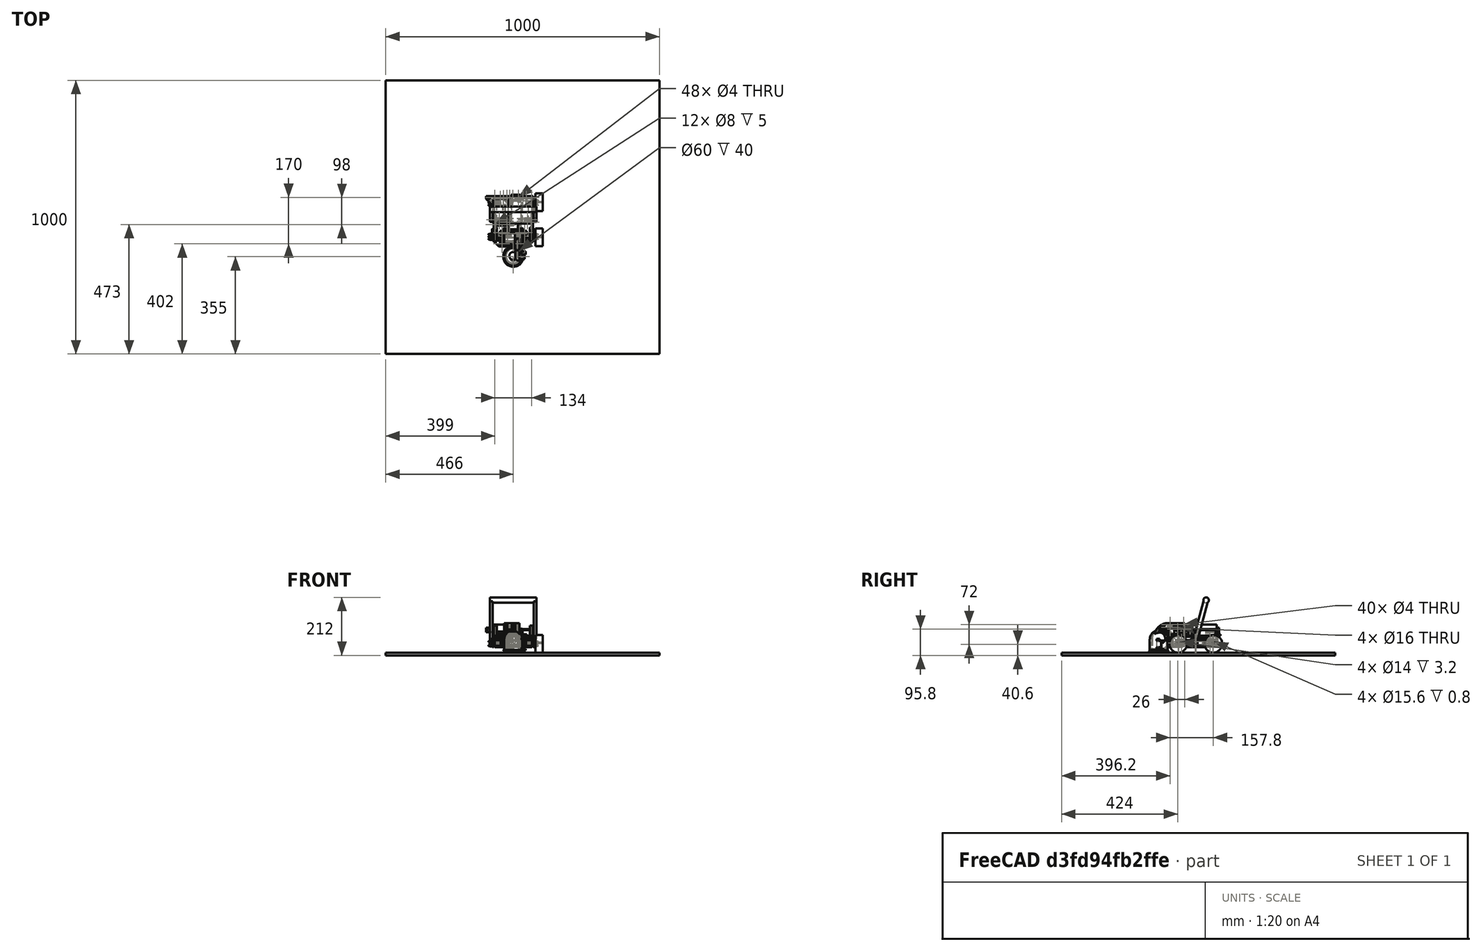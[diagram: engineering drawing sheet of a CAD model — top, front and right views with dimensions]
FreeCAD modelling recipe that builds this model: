
FCSTD DOCUMENT  (FreeCAD 1.0R39109 (Git))
Label: robot - robcup-ber3.2
License: All rights reserved
LicenseURL: https://en.wikipedia.org/wiki/All_rights_reserved
objects: Part::Cylinder×204, Part::Box×156, Part::Cut×138, Part::MultiFuse×132, Part::FeaturePython×20, Part::Chamfer×15, Part::Sphere×10, Part::Fillet×10, Part::Cone×6, Part::Extrusion×4, Part::Part2DObjectPython×2, Part::Fuse×2, Part::RuledSurface×2
note: 701 computed .brp shape members not serialized (recipe doc carries the construction recipe); baked Part::Feature solids carry a one-line shape summary decoded from their .brp

FEATURE [Part::Box] Box001  label="rasbperry pi"
  AttacherType = Attacher::AttachEngine3D
  Height = 25
  Length = 56
  Placement = pos=(-108,-22,52) rot=(0,0,1;0rad)
  Width = 88
FEATURE [Part::Box] Box024  label="立方体004"
  AttacherType = Attacher::AttachEngine3D
  Height = 25
  Length = 51
  Placement = pos=(-51,-93,16) rot=(0,0,1;0rad)
  Width = 5
FEATURE [Part::Box] Box025  label="立方体005"
  AttacherType = Attacher::AttachEngine3D
  Height = 25
  Length = 23
  Placement = pos=(-37,-93,16) rot=(0,0,1;0rad)
  Width = 5
FEATURE [Part::Box] Box026  label="立方体006"
  AttacherType = Attacher::AttachEngine3D
  Height = 10
  Length = 51
  Placement = pos=(-51,-90,31) rot=(0,0,1;0rad)
  Width = 5
FEATURE [Part::Box] Box027  label="立方体007"
  AttacherType = Attacher::AttachEngine3D
  Height = 20.4
  Length = 45.2
  Placement = pos=(-48.6,-98,10) rot=(0,0,1;0rad)
  Width = 5
FEATURE [Part::Cylinder] Cylinder004  label="円柱004"
  Angle = 360
  AttacherType = Attacher::AttachEngine3D
  FirstAngle = 0
  Height = 15
  Placement = pos=(-13,-93,20.2) rot=(1,0,0;1.5708rad)
  Radius = 8
  SecondAngle = 0
FEATURE [Part::Cylinder] Cylinder005  label="円柱005"
  Angle = 360
  AttacherType = Attacher::AttachEngine3D
  FirstAngle = 0
  Height = 15
  Placement = pos=(-39,-93,20.2) rot=(1,0,0;1.5708rad)
  Radius = 8
  SecondAngle = 0
FEATURE [Part::Cylinder] Cylinder007  label="円柱007"
  Angle = 360
  AttacherType = Attacher::AttachEngine3D
  FirstAngle = 0
  Height = 32
  Placement = pos=(0,82,0) rot=(0,0,1;0rad)
  Radius = 4
  SecondAngle = 0
FEATURE [Part::Cylinder] Cylinder011  label="円柱011"
  Angle = 360
  AttacherType = Attacher::AttachEngine3D
  FirstAngle = 0
  Height = 32
  Placement = pos=(15.2,-98,0) rot=(0,0,1;0rad)
  Radius = 4
  SecondAngle = 0
FEATURE [Part::Cylinder] Cylinder012  label="円柱012"
  Angle = 360
  AttacherType = Attacher::AttachEngine3D
  FirstAngle = 0
  Height = 42
  Placement = pos=(-68,82,-5) rot=(0,0,1;0rad)
  Radius = 2
  SecondAngle = 0
FEATURE [Part::Cylinder] Cylinder016  label="円柱016"
  Angle = 360
  AttacherType = Attacher::AttachEngine3D
  FirstAngle = 0
  Height = 32
  Placement = pos=(-83,-98,0) rot=(0,0,1;0rad)
  Radius = 4
  SecondAngle = 0
FEATURE [Part::Box] Box060  label="（バッテリー）"
  AttacherType = Attacher::AttachEngine3D
  Height = 26.5
  Length = 58
  Placement = pos=(-62.9,-27,0) rot=(0,0,1;0rad)
  Width = 81.5
FEATURE [Part::Box] Box069  label="立方体048"
  AttacherType = Attacher::AttachEngine3D
  Height = 20.1
  Length = 38.8
  Placement = pos=(82,-93,0) rot=(0,0,1;0rad)
  Width = 40.1
FEATURE [Part::Box] Box075  label="立方体054"
  AttacherType = Attacher::AttachEngine3D
  Height = 20.1
  Length = 38.8
  Placement = pos=(82,-93,0) rot=(0,0,1;0rad)
  Width = 40.1
FEATURE [Part::Box] Box084  label="立方体063"
  AttacherType = Attacher::AttachEngine3D
  Height = 20.1
  Length = 2.7
  Placement = pos=(90.8,-99.95,0) rot=(0,0,1;0rad)
  Width = 54
FEATURE [Part::MultiFuse] Fusion040
  Placement = pos=(-7.9,-3,-13) rot=(0,0,1;0rad)
  Refine = true
  Shapes = -> [Box027,Cylinder004,Cylinder005]
FEATURE [Part::Box] Box097  label="立方体076"
  AttacherType = Attacher::AttachEngine3D
  Height = 25
  Length = 52
  Placement = pos=(-60,-93,16) rot=(0,0,1;0rad)
  Width = 5
FEATURE [Part::Box] Box098  label="立方体077"
  AttacherType = Attacher::AttachEngine3D
  Height = 25
  Length = 35
  Placement = pos=(-52,-88,16) rot=(0,0,1;0rad)
  Width = 5
FEATURE [Part::Box] Box100  label="立方体079"
  AttacherType = Attacher::AttachEngine3D
  Height = 25
  Length = 25
  Placement = pos=(-38.5,-94,16) rot=(0,0,1;0rad)
  Width = 1
FEATURE [Part::Box] Box101  label="立方体080"
  AttacherType = Attacher::AttachEngine3D
  Height = 25
  Length = 15
  Placement = pos=(-33.5,-101,16) rot=(0,0,1;0rad)
  Width = 7
FEATURE [Part::Box] Box102  label="立方体081"
  AttacherType = Attacher::AttachEngine3D
  Height = 5
  Length = 60
  Placement = pos=(-63.9,-96,-5) rot=(0,0,1;0rad)
  Width = 64
FEATURE [Part::Cylinder] Cylinder033  label="円柱033"
  Angle = 360
  AttacherType = Attacher::AttachEngine3D
  FirstAngle = 0
  Height = 32
  Placement = pos=(30.2,-10,0) rot=(0,0,1;0rad)
  Radius = 4
  SecondAngle = 0
FEATURE [Part::Cylinder] Cylinder034  label="円柱034"
  Angle = 360
  AttacherType = Attacher::AttachEngine3D
  FirstAngle = 0
  Height = 32
  Placement = pos=(-98,-10,0) rot=(0,0,1;0rad)
  Radius = 4
  SecondAngle = 0
FEATURE [Part::Box] Box213  label="立方体191"
  AttacherType = Attacher::AttachEngine3D
  Height = 12
  Length = 3
  Placement = pos=(-65.9,-16.9,0) rot=(0,0,1;0rad)
  Width = 13.9
FEATURE [Part::Box] Box214  label="立方体192"
  AttacherType = Attacher::AttachEngine3D
  Height = 12
  Length = 3
  Placement = pos=(-4.9,-16.9,0) rot=(0,0,1;0rad)
  Width = 13.9
FEATURE [Part::Box] Box215  label="立方体193"
  AttacherType = Attacher::AttachEngine3D
  Height = 5
  Length = 54
  Placement = pos=(-60.9,-108,32) rot=(0,0,1;0rad)
  Width = 71
FEATURE [Part::Box] Box223  label="立方体201"
  AttacherType = Attacher::AttachEngine3D
  Height = 20.1
  Length = 2.7
  Placement = pos=(90.8,-99.95,0) rot=(0,0,1;0rad)
  Width = 54
FEATURE [Part::Box] Box225  label="立方体203"
  AttacherType = Attacher::AttachEngine3D
  Height = 20.1
  Length = 2.7
  Placement = pos=(109.3,-99.95,0) rot=(0,0,1;0rad)
  Width = 54
FEATURE [Part::MultiFuse] Fusion084
  Placement = pos=(-188,26,0) rot=(0,0,1;0rad)
  Shapes = -> [Box084,Box069]
FEATURE [Part::MultiFuse] Fusion085
  Placement = pos=(-188,100,0) rot=(0,0,1;0rad)
  Shapes = -> [Box223,Box075]
FEATURE [Part::Box] Box226  label="立方体204"
  AttacherType = Attacher::AttachEngine3D
  Height = 20.1
  Length = 38.8
  Placement = pos=(82,-93,0) rot=(0,0,1;0rad)
  Width = 40.1
FEATURE [Part::Box] Box227  label="立方体205"
  AttacherType = Attacher::AttachEngine3D
  Height = 20.1
  Length = 38.8
  Placement = pos=(82,-93,0) rot=(0,0,1;0rad)
  Width = 40.1
FEATURE [Part::MultiFuse] Fusion086
  Placement = pos=(-82.6,26,0) rot=(0,0,1;0rad)
  Shapes = -> [Box226,Box225]
FEATURE [Part::Box] Box076  label="立方体055"
  AttacherType = Attacher::AttachEngine3D
  Height = 20.1
  Length = 2.7
  Placement = pos=(109.3,-99.95,0) rot=(0,0,1;0rad)
  Width = 54
FEATURE [Part::MultiFuse] Fusion087
  Placement = pos=(-82.6,100,0) rot=(0,0,1;0rad)
  Shapes = -> [Box076,Box227]
FEATURE [Part::Box] Box229  label="立方体208"
  AttacherType = Attacher::AttachEngine3D
  Height = 20
  Length = 10
  Placement = pos=(16.7,47.1,0) rot=(0,0,1;0rad)
  Width = 7
FEATURE [Part::Box] Box235  label="立方体214"
  AttacherType = Attacher::AttachEngine3D
  Height = 12
  Length = 58.6
  Placement = pos=(-63.2,-30,0) rot=(0,0,1;0rad)
  Width = 3
FEATURE [Part::Box] Box242  label="立方体220"
  AttacherType = Attacher::AttachEngine3D
  Height = 20
  Length = 21.5
  Placement = pos=(16,57.1,0) rot=(0,0,1;0rad)
  Width = 13
FEATURE [Part::Box] Box254  label="立方体229"
  AttacherType = Attacher::AttachEngine3D
  Height = 22
  Length = 54
  Placement = pos=(-60.9,-108,-3) rot=(0,0,1;0rad)
  Width = 12
FEATURE [Part::FeaturePython] CycloidGear  # WARN: FeaturePython — macro-defined, semantics opaque (R4)
  AttacherType = Attacher::AttachEngine3D
  Placement = pos=(-32.8,-91,71) rot=(0,1,0;1.5708rad)
  angular_backlash = 0
  backlash = 0
  clearance = 0.25
  double_helix = false
  head = 0
  head_fillet = 0
  height = 5.5
  helix_angle = 0
  inner_diameter = 12.5
  module = 0.24
  num_teeth = 25
  numpoints = 20
  outer_diameter = 7.5
  pitch_diameter = 6
  root_fillet = 0
  version = 1.3.0
  expr: angular_backlash = backlash / pitch_diameter * 360 ° / pi
  expr: inner_diameter = num_teeth / 2
  expr: pitch_diameter = num_teeth * module
FEATURE [Part::Box] Box259  label="立方体234"
  AttacherType = Attacher::AttachEngine3D
  Height = 3
  Length = 90
  Placement = pos=(-52,-40,42) rot=(0,0,1;0rad)
  Width = 100
FEATURE [Part::Box] Box260  label="立方体235"
  AttacherType = Attacher::AttachEngine3D
  Height = 3
  Length = 56
  Placement = pos=(-104,-22,37) rot=(0,0,1;0rad)
  Width = 88
FEATURE [Part::Cylinder] Cylinder064  label="円柱064"
  Angle = 360
  AttacherType = Attacher::AttachEngine3D
  FirstAngle = 0
  Height = 3
  Placement = pos=(-100.5,62.5,37) rot=(0,0,1;0rad)
  Radius = 1.25
  SecondAngle = 0
FEATURE [Part::Cylinder] Cylinder065  label="円柱065"
  Angle = 360
  AttacherType = Attacher::AttachEngine3D
  FirstAngle = 0
  Height = 3
  Placement = pos=(-51.5,62.5,37) rot=(0,0,1;0rad)
  Radius = 1.25
  SecondAngle = 0
FEATURE [Part::Cylinder] Cylinder066  label="円柱066"
  Angle = 360
  AttacherType = Attacher::AttachEngine3D
  FirstAngle = 0
  Height = 3
  Placement = pos=(-51.5,4.5,37) rot=(0,0,1;0rad)
  Radius = 1.25
  SecondAngle = 0
FEATURE [Part::Cylinder] Cylinder067  label="円柱067"
  Angle = 360
  AttacherType = Attacher::AttachEngine3D
  FirstAngle = 0
  Height = 3
  Placement = pos=(-100.5,4.5,37) rot=(0,0,1;0rad)
  Radius = 1.25
  SecondAngle = 0
FEATURE [Part::Box] Box263  label="立方体237"
  AttacherType = Attacher::AttachEngine3D
  Height = 20.4
  Length = 45.2
  Placement = pos=(-48.6,-98,10) rot=(0,0,1;0rad)
  Width = 5
FEATURE [Part::Cylinder] Cylinder068  label="円柱068"
  Angle = 360
  AttacherType = Attacher::AttachEngine3D
  FirstAngle = 0
  Height = 15
  Placement = pos=(-13,-93,20.2) rot=(1,0,0;1.5708rad)
  Radius = 8
  SecondAngle = 0
FEATURE [Part::Cylinder] Cylinder069  label="円柱069"
  Angle = 360
  AttacherType = Attacher::AttachEngine3D
  FirstAngle = 0
  Height = 15
  Placement = pos=(-39,-93,20.2) rot=(1,0,0;1.5708rad)
  Radius = 8
  SecondAngle = 0
FEATURE [Part::MultiFuse] Fusion112
  Placement = pos=(-1,-109,40) rot=(0,0,-1;1.5708rad)
  Refine = true
  Shapes = -> [Box263,Cylinder069,Cylinder068]
FEATURE [Part::Box] Box264  label="立方体238"
  AttacherType = Attacher::AttachEngine3D
  Height = 20.4
  Length = 45.2
  Placement = pos=(-48.6,-98,10) rot=(0,0,1;0rad)
  Width = 5
FEATURE [Part::Cylinder] Cylinder070  label="円柱070"
  Angle = 360
  AttacherType = Attacher::AttachEngine3D
  FirstAngle = 0
  Height = 15
  Placement = pos=(-13,-93,20.2) rot=(1,0,0;1.5708rad)
  Radius = 8
  SecondAngle = 0
FEATURE [Part::Cylinder] Cylinder071  label="円柱071"
  Angle = 360
  AttacherType = Attacher::AttachEngine3D
  FirstAngle = 0
  Height = 15
  Placement = pos=(-39,-93,20.2) rot=(1,0,0;1.5708rad)
  Radius = 8
  SecondAngle = 0
FEATURE [Part::MultiFuse] Fusion113
  Placement = pos=(-66.8,-57,40) rot=(0,0,1;1.5708rad)
  Refine = true
  Shapes = -> [Box264,Cylinder071,Cylinder070]
FEATURE [Part::Box] Box266  label="立方体240"
  AttacherType = Attacher::AttachEngine3D
  Height = 50
  Length = 12
  Placement = pos=(-106,-58,37) rot=(1,0,0;1.5708rad)
  Width = 36
FEATURE [Part::Box] Box268  label="立方体242"
  AttacherType = Attacher::AttachEngine3D
  Height = 50
  Length = 12
  Placement = pos=(26.2,-58,37) rot=(1,0,0;1.5708rad)
  Width = 36
FEATURE [Part::Box] Box270  label="地面"
  AttacherType = Attacher::AttachEngine3D
  Height = 10
  Length = 1000
  Placement = pos=(-500,-500,-35.6) rot=(0,0,1;0rad)
  Width = 1000
FEATURE [Part::Cylinder] Cylinder072  label="円柱072"
  Angle = 360
  AttacherType = Attacher::AttachEngine3D
  FirstAngle = 0
  Height = 40.5
  Placement = pos=(-125,62,10) rot=(0,1,0;1.5708rad)
  Radius = 4
  SecondAngle = 0
FEATURE [Part::FeaturePython] CycloidGear001  # WARN: FeaturePython — macro-defined, semantics opaque (R4)
  AttacherType = Attacher::AttachEngine3D
  Placement = pos=(-111.4,62,10) rot=(0,1,0;1.5708rad)
  angular_backlash = 0
  backlash = 0
  clearance = 0.25
  double_helix = false
  head = 0
  head_fillet = 0
  height = 4
  helix_angle = 0
  inner_diameter = 12.5
  module = 1
  num_teeth = 25
  numpoints = 20
  outer_diameter = 7.5
  pitch_diameter = 25
  root_fillet = 0
  version = 1.3.0
  expr: angular_backlash = backlash / pitch_diameter * 360 ° / pi
  expr: inner_diameter = num_teeth / 2
  expr: pitch_diameter = num_teeth * module
FEATURE [Part::FeaturePython] CycloidGear002  # WARN: FeaturePython — macro-defined, semantics opaque (R4)
  AttacherType = Attacher::AttachEngine3D
  Placement = pos=(-111.45,37,10) rot=(0,1,0;1.5708rad)
  angular_backlash = 0
  backlash = 0
  clearance = 0.25
  double_helix = false
  head = 0
  head_fillet = 0
  height = 4
  helix_angle = 0
  inner_diameter = 12.5
  module = 1
  num_teeth = 25
  numpoints = 20
  outer_diameter = 7.5
  pitch_diameter = 25
  root_fillet = 0
  version = 1.3.0
  expr: angular_backlash = backlash / pitch_diameter * 360 ° / pi
  expr: inner_diameter = num_teeth / 2
  expr: pitch_diameter = num_teeth * module
FEATURE [Part::FeaturePython] CycloidGear003  # WARN: FeaturePython — macro-defined, semantics opaque (R4)
  AttacherType = Attacher::AttachEngine3D
  Placement = pos=(-111.45,37,10) rot=(0,1,0;1.5708rad)
  angular_backlash = 0
  backlash = 0
  clearance = 0.25
  double_helix = false
  head = 0
  head_fillet = 0
  height = 4
  helix_angle = 0
  inner_diameter = 12.5
  module = 0.24
  num_teeth = 25
  numpoints = 20
  outer_diameter = 7.5
  pitch_diameter = 6
  root_fillet = 0
  version = 1.3.0
  expr: angular_backlash = backlash / pitch_diameter * 360 ° / pi
  expr: inner_diameter = num_teeth / 2
  expr: pitch_diameter = num_teeth * module
FEATURE [Part::Sphere] Sphere  label="球体"
  Angle1 = 0
  Angle2 = 60
  Angle3 = 360
  AttacherType = Attacher::AttachEngine3D
  Placement = pos=(-34,-160,45) rot=(0,0,1;0rad)
  Radius = 33
FEATURE [Part::Sphere] Sphere001  label="球体001"
  Angle1 = 0
  Angle2 = 60
  Angle3 = 360
  AttacherType = Attacher::AttachEngine3D
  Placement = pos=(-34,-160,45) rot=(0,0,1;0rad)
  Radius = 30
FEATURE [Part::Cone] Cone  label="円錐"
  Angle = 360
  AttacherType = Attacher::AttachEngine3D
  Height = 5
  Radius1 = 38
  Radius2 = 33
FEATURE [Part::Cone] Cone001  label="円錐001"
  Angle = 360
  AttacherType = Attacher::AttachEngine3D
  Height = 5
  Radius1 = 33
  Radius2 = 30
FEATURE [Part::Cut] Cut053
  Base = -> Cone
  Placement = pos=(-34,-160,0) rot=(0,0,1;0rad)
  Tool = -> Cone001
FEATURE [Part::Chamfer] Chamfer016
  Base = -> Cut053
  EdgeLinks = -> Cut053 [Edge3]
  Edges = 1 edges r=2: [Edge3]
FEATURE [Part::Cylinder] Cylinder073  label="円柱073"
  Angle = 360
  AttacherType = Attacher::AttachEngine3D
  FirstAngle = 0
  Height = 20
  Placement = pos=(-60,-160,-3) rot=(0,-1,0;0.785398rad)
  Radius = 1
  SecondAngle = 0
FEATURE [Part::Cylinder] Cylinder074  label="円柱074"
  Angle = 360
  AttacherType = Attacher::AttachEngine3D
  FirstAngle = 0
  Height = 20
  Placement = pos=(-8,-160,-3) rot=(0,1,0;0.785398rad)
  Radius = 1
  SecondAngle = 0
FEATURE [Part::Box] Box273  label="立方体246"
  AttacherType = Attacher::AttachEngine3D
  Height = 20.1
  Length = 2.7
  Placement = pos=(109.3,-99.95,0) rot=(0,0,1;0rad)
  Width = 54
FEATURE [Part::Box] Box274  label="立方体247"
  AttacherType = Attacher::AttachEngine3D
  Height = 20.1
  Length = 38.8
  Placement = pos=(82,-93,0) rot=(0,0,1;0rad)
  Width = 40.1
FEATURE [Part::MultiFuse] Fusion118
  Placement = pos=(-153.6,-8,61) rot=(0,0,1;0rad)
  Shapes = -> [Box274,Box273]
FEATURE [Part::Cylinder] Cylinder076  label="円柱076"
  Angle = 360
  AttacherType = Attacher::AttachEngine3D
  FirstAngle = 0
  Height = 50
  Placement = pos=(-34,-160,-17) rot=(0,0,1;0rad)
  Radius = 33
  SecondAngle = 0
FEATURE [Part::Box] Box278  label="立方体250"
  AttacherType = Attacher::AttachEngine3D
  Height = 35
  Length = 45.1
  Placement = pos=(-34,-146,-17) rot=(0,0,1;0rad)
  Width = 25
FEATURE [Part::Box] Box279  label="立方体251"
  AttacherType = Attacher::AttachEngine3D
  Height = 32.3
  Length = 12.1
  Placement = pos=(0,8.5,-4.9) rot=(0,0,1;0rad)
  Width = 2.5
FEATURE [Part::Box] Box280  label="立方体252"
  AttacherType = Attacher::AttachEngine3D
  Height = 22.5
  Length = 12.1
  Width = 26.7
FEATURE [Part::Cylinder] Cylinder077  label="円柱077"
  Angle = 360
  AttacherType = Attacher::AttachEngine3D
  FirstAngle = 0
  Height = 3
  Placement = pos=(6.05,0,16.4) rot=(1,0,0;1.5708rad)
  Radius = 2.4
  SecondAngle = 0
FEATURE [Part::MultiFuse] Fusion120
  Placement = pos=(-1,-151,-12) rot=(0,0,1;0rad)
  Shapes = -> [Cylinder077,Box279,Box280]
FEATURE [Part::Cut] Cut056
  Base = -> Box278
  Tool = -> Fusion120
FEATURE [Part::Cut] Cut057
  Base = -> Cut056
  Placement = pos=(0,15,-3) rot=(0,0,1;0rad)
  Tool = -> Cylinder076
FEATURE [Part::MultiFuse] Fusion121
  Placement = pos=(0,0,-3) rot=(0,0,1;0rad)
  Shapes = -> [Fusion118,CycloidGear]
FEATURE [Part::Box] Box281  label="立方体253"
  AttacherType = Attacher::AttachEngine3D
  Height = 20.1
  Length = 27.3
  Placement = pos=(-71.6,-108,62) rot=(0,0,1;0rad)
  Width = 9
FEATURE [Part::Box] Box283  label="立方体255"
  AttacherType = Attacher::AttachEngine3D
  Height = 3
  Length = 66
  Placement = pos=(-71.6,-108,59) rot=(0,0,1;0rad)
  Width = 58.1
FEATURE [Part::Box] Box286  label="立方体258"
  AttacherType = Attacher::AttachEngine3D
  Height = 25
  Length = 6
  Placement = pos=(-66.9,-108,37) rot=(0,0,1;0rad)
  Width = 20
FEATURE [Part::Box] Box288  label="立方体260"
  AttacherType = Attacher::AttachEngine3D
  Height = 25
  Length = 6
  Placement = pos=(-6.9,-108,37) rot=(0,0,1;0rad)
  Width = 20
FEATURE [Part::Cylinder] Cylinder083  label="円柱083"
  Angle = 360
  AttacherType = Attacher::AttachEngine3D
  FirstAngle = 0
  Height = 15
  Placement = pos=(-31.3,-89,72) rot=(0.57735,0.57735,0.57735;2.0944rad)
  Radius = 10
  SecondAngle = 0
FEATURE [Part::Box] Box289  label="立方体261"
  AttacherType = Attacher::AttachEngine3D
  Height = 20
  Length = 15
  Placement = pos=(-31.3,-112,62) rot=(0,0,1;0rad)
  Width = 23
FEATURE [Part::Cylinder] Cylinder084  label="円柱084"
  Angle = 360
  AttacherType = Attacher::AttachEngine3D
  FirstAngle = 0
  Height = 50
  Placement = pos=(-34,-145,-27) rot=(0,0,1;0rad)
  Radius = 30
  SecondAngle = 0
FEATURE [Part::Sphere] Sphere003  label="球体003"
  Angle1 = 0
  Angle2 = 60
  Angle3 = 360
  AttacherType = Attacher::AttachEngine3D
  Placement = pos=(-34,-145,23) rot=(0,0,1;0rad)
  Radius = 30
FEATURE [Part::Cylinder] Cylinder085  label="円柱085"
  Angle = 360
  AttacherType = Attacher::AttachEngine3D
  FirstAngle = 0
  Height = 5
  Placement = pos=(-128.4,53.35,15) rot=(0,1,0;1.5708rad)
  Radius = 1.5
  SecondAngle = 0
FEATURE [Part::FeaturePython] Tube  # WARN: FeaturePython — macro-defined, semantics opaque (R4)
  AttacherType = Attacher::AttachEngine3D
  Height = 2
  InnerRadius = 6
  OuterRadius = 15
  Placement = pos=(-113.4,62,10) rot=(0,1,0;1.5708rad)
FEATURE [Part::Cylinder] Cylinder086  label="円柱086"
  Angle = 360
  AttacherType = Attacher::AttachEngine3D
  FirstAngle = 0
  Height = 5
  Placement = pos=(-128.4,70.66,15) rot=(0,1,0;1.5708rad)
  Radius = 1.5
  SecondAngle = 0
FEATURE [Part::Cylinder] Cylinder087  label="円柱087"
  Angle = 360
  AttacherType = Attacher::AttachEngine3D
  FirstAngle = 0
  Height = 5
  Placement = pos=(-128.4,62,0) rot=(0,1,0;1.5708rad)
  Radius = 1.5
  SecondAngle = 0
FEATURE [Part::FeaturePython] CycloidGear004  # WARN: FeaturePython — macro-defined, semantics opaque (R4)
  AttacherType = Attacher::AttachEngine3D
  Placement = pos=(39.6,62,10) rot=(0,1,0;1.5708rad)
  angular_backlash = 0
  backlash = 0
  clearance = 0.25
  double_helix = false
  head = 0
  head_fillet = 0
  height = 4
  helix_angle = 0
  inner_diameter = 12.5
  module = 1
  num_teeth = 25
  numpoints = 20
  outer_diameter = 7.5
  pitch_diameter = 25
  root_fillet = 0
  version = 1.3.0
  expr: angular_backlash = backlash / pitch_diameter * 360 ° / pi
  expr: inner_diameter = num_teeth / 2
  expr: pitch_diameter = num_teeth * module
FEATURE [Part::Cut] Cut062  label="右下モーター側ギア"
  Base = -> CycloidGear002
  Placement = pos=(4,-10,0) rot=(0,0,1;0rad)
  Tool = -> CycloidGear003
FEATURE [Part::FeaturePython] CycloidGear007  # WARN: FeaturePython — macro-defined, semantics opaque (R4)
  AttacherType = Attacher::AttachEngine3D
  Placement = pos=(-111.45,37,10) rot=(0,1,0;1.5708rad)
  angular_backlash = 0
  backlash = 0
  clearance = 0.25
  double_helix = false
  head = 0
  head_fillet = 0
  height = 4
  helix_angle = 0
  inner_diameter = 12.5
  module = 1
  num_teeth = 25
  numpoints = 20
  outer_diameter = 7.5
  pitch_diameter = 25
  root_fillet = 0
  version = 1.3.0
  expr: angular_backlash = backlash / pitch_diameter * 360 ° / pi
  expr: inner_diameter = num_teeth / 2
  expr: pitch_diameter = num_teeth * module
FEATURE [Part::FeaturePython] CycloidGear008  # WARN: FeaturePython — macro-defined, semantics opaque (R4)
  AttacherType = Attacher::AttachEngine3D
  Placement = pos=(-111.45,37,10) rot=(0,1,0;1.5708rad)
  angular_backlash = 0
  backlash = 0
  clearance = 0.25
  double_helix = false
  head = 0
  head_fillet = 0
  height = 4
  helix_angle = 0
  inner_diameter = 12.5
  module = 0.24
  num_teeth = 25
  numpoints = 20
  outer_diameter = 7.5
  pitch_diameter = 6
  root_fillet = 0
  version = 1.3.0
  expr: angular_backlash = backlash / pitch_diameter * 360 ° / pi
  expr: inner_diameter = num_teeth / 2
  expr: pitch_diameter = num_teeth * module
FEATURE [Part::Cut] Cut064  label="左下モーター側ギア"
  Base = -> CycloidGear007
  Placement = pos=(151.05,0,0) rot=(0,0,1;0rad)
  Tool = -> CycloidGear008
FEATURE [Part::Cylinder] Cylinder088  label="円柱088"
  Angle = 360
  AttacherType = Attacher::AttachEngine3D
  FirstAngle = 0
  Height = 10
  Placement = pos=(-123.4,70.66,15) rot=(0,1,0;1.5708rad)
  Radius = 3
  SecondAngle = 0
FEATURE [Part::Cylinder] Cylinder089  label="円柱089"
  Angle = 360
  AttacherType = Attacher::AttachEngine3D
  FirstAngle = 0
  Height = 10
  Placement = pos=(-123.4,-90.65,15) rot=(0,1,0;1.5708rad)
  Radius = 3
  SecondAngle = 0
FEATURE [Part::Cylinder] Cylinder090  label="円柱090"
  Angle = 360
  AttacherType = Attacher::AttachEngine3D
  FirstAngle = 0
  Height = 10
  Placement = pos=(-123.4,62,0) rot=(0,1,0;1.5708rad)
  Radius = 3
  SecondAngle = 0
FEATURE [Part::Box] Box294  label="立方体266"
  AttacherType = Attacher::AttachEngine3D
  Height = 3
  Length = 3
  Placement = pos=(-57,-22,37) rot=(0,0,1;0rad)
  Width = 68
FEATURE [Part::Box] Box296  label="立方体268"
  AttacherType = Attacher::AttachEngine3D
  Height = 3
  Length = 36
  Placement = pos=(-90,43,37) rot=(0,0,1;0rad)
  Width = 3
FEATURE [Part::Box] Box297  label="立方体269"
  AttacherType = Attacher::AttachEngine3D
  Height = 13
  Length = 30
  Placement = pos=(-94,-22,34) rot=(0,0,1;0rad)
  Width = 65
FEATURE [Part::Box] Box298  label="立方体270"
  AttacherType = Attacher::AttachEngine3D
  Height = 12
  Length = 10
  Placement = pos=(-62,66,37) rot=(0,0,1;0rad)
  Width = 10
FEATURE [Part::Box] Box299  label="立方体271"
  AttacherType = Attacher::AttachEngine3D
  Height = 12
  Length = 10
  Placement = pos=(-62,-32,37) rot=(0,0,1;0rad)
  Width = 10
FEATURE [Part::Box] Box300  label="立方体272"
  AttacherType = Attacher::AttachEngine3D
  Height = 12
  Length = 10
  Placement = pos=(-106,-32,37) rot=(0,0,1;0rad)
  Width = 10
FEATURE [Part::Box] Box301  label="立方体273"
  AttacherType = Attacher::AttachEngine3D
  Height = 12
  Length = 10
  Placement = pos=(-106,66,37) rot=(0,0,1;0rad)
  Width = 10
FEATURE [Part::Cylinder] Cylinder091  label="円柱091"
  Angle = 360
  AttacherType = Attacher::AttachEngine3D
  FirstAngle = 0
  Height = 1.4
  Placement = pos=(-107.4,62,10) rot=(0,1,0;1.5708rad)
  Radius = 5
  SecondAngle = 0
FEATURE [Part::Box] Box302  label="立方体274"
  AttacherType = Attacher::AttachEngine3D
  Height = 20
  Length = 21.5
  Placement = pos=(-106,-90,0) rot=(0,0,1;0rad)
  Width = 13
FEATURE [Part::Cylinder] Cylinder093  label="円柱093"
  Angle = 360
  AttacherType = Attacher::AttachEngine3D
  FirstAngle = 0
  Height = 40.5
  Placement = pos=(-125,-82,10) rot=(0,1,0;1.5708rad)
  Radius = 4
  SecondAngle = 0
FEATURE [Part::FeaturePython] CycloidGear009  # WARN: FeaturePython — macro-defined, semantics opaque (R4)
  AttacherType = Attacher::AttachEngine3D
  Placement = pos=(-111.4,-82,10) rot=(0,1,0;1.5708rad)
  angular_backlash = 0
  backlash = 0
  clearance = 0.25
  double_helix = false
  head = 0
  head_fillet = 0
  height = 4
  helix_angle = 0
  inner_diameter = 12.5
  module = 1
  num_teeth = 25
  numpoints = 20
  outer_diameter = 7.5
  pitch_diameter = 25
  root_fillet = 0
  version = 1.3.0
  expr: angular_backlash = backlash / pitch_diameter * 360 ° / pi
  expr: inner_diameter = num_teeth / 2
  expr: pitch_diameter = num_teeth * module
FEATURE [Part::FeaturePython] Tube014  # WARN: FeaturePython — macro-defined, semantics opaque (R4)
  AttacherType = Attacher::AttachEngine3D
  Height = 2
  InnerRadius = 6
  OuterRadius = 15
  Placement = pos=(-113.4,-82,10) rot=(0,1,0;1.5708rad)
FEATURE [Part::Cylinder] Cylinder100  label="円柱100"
  Angle = 360
  AttacherType = Attacher::AttachEngine3D
  FirstAngle = 0
  Height = 10
  Placement = pos=(-123.4,53.35,15) rot=(0,1,0;1.5708rad)
  Radius = 3
  SecondAngle = 0
FEATURE [Part::Cylinder] Cylinder101  label="円柱101"
  Angle = 360
  AttacherType = Attacher::AttachEngine3D
  FirstAngle = 0
  Height = 10
  Placement = pos=(-123.4,-73.34,15) rot=(0,1,0;1.5708rad)
  Radius = 3
  SecondAngle = 0
FEATURE [Part::Cylinder] Cylinder102  label="円柱102"
  Angle = 360
  AttacherType = Attacher::AttachEngine3D
  FirstAngle = 0
  Height = 10
  Placement = pos=(-123.4,-82,0) rot=(0,1,0;1.5708rad)
  Radius = 3
  SecondAngle = 0
FEATURE [Part::Cylinder] Cylinder106  label="円柱106"
  Angle = 360
  AttacherType = Attacher::AttachEngine3D
  FirstAngle = 0
  Height = 1.4
  Placement = pos=(-107.4,-82,10) rot=(0,1,0;1.5708rad)
  Radius = 5
  SecondAngle = 0
FEATURE [Part::FeaturePython] CycloidGear010  # WARN: FeaturePython — macro-defined, semantics opaque (R4)
  AttacherType = Attacher::AttachEngine3D
  Placement = pos=(-111.45,37,10) rot=(0,1,0;1.5708rad)
  angular_backlash = 0
  backlash = 0
  clearance = 0.25
  double_helix = false
  head = 0
  head_fillet = 0
  height = 4
  helix_angle = 0
  inner_diameter = 12.5
  module = 1
  num_teeth = 25
  numpoints = 20
  outer_diameter = 7.5
  pitch_diameter = 25
  root_fillet = 0
  version = 1.3.0
  expr: angular_backlash = backlash / pitch_diameter * 360 ° / pi
  expr: inner_diameter = num_teeth / 2
  expr: pitch_diameter = num_teeth * module
FEATURE [Part::FeaturePython] CycloidGear011  # WARN: FeaturePython — macro-defined, semantics opaque (R4)
  AttacherType = Attacher::AttachEngine3D
  Placement = pos=(-111.45,37,10) rot=(0,1,0;1.5708rad)
  angular_backlash = 0
  backlash = 0
  clearance = 0.25
  double_helix = false
  head = 0
  head_fillet = 0
  height = 4
  helix_angle = 0
  inner_diameter = 12.5
  module = 0.24
  num_teeth = 25
  numpoints = 20
  outer_diameter = 7.5
  pitch_diameter = 6
  root_fillet = 0
  version = 1.3.0
  expr: angular_backlash = backlash / pitch_diameter * 360 ° / pi
  expr: inner_diameter = num_teeth / 2
  expr: pitch_diameter = num_teeth * module
FEATURE [Part::Cut] Cut073  label="右上モーター側ギア"
  Base = -> CycloidGear010
  Placement = pos=(0.05,-94,0) rot=(0,0,1;0rad)
  Tool = -> CycloidGear011
FEATURE [Part::FeaturePython] Tube017  # WARN: FeaturePython — macro-defined, semantics opaque (R4)
  AttacherType = Attacher::AttachEngine3D
  Height = 2
  InnerRadius = 6
  OuterRadius = 15
  Placement = pos=(43.6,62,10) rot=(0,1,0;1.5708rad)
FEATURE [Part::Cylinder] Cylinder108  label="円柱108"
  Angle = 360
  AttacherType = Attacher::AttachEngine3D
  FirstAngle = 0
  Height = 1.4
  Placement = pos=(38.2,62,10) rot=(0,1,0;1.5708rad)
  Radius = 5
  SecondAngle = 0
FEATURE [Part::Cylinder] Cylinder109  label="円柱109"
  Angle = 360
  AttacherType = Attacher::AttachEngine3D
  FirstAngle = 0
  Height = 10
  Placement = pos=(45.6,70.66,15) rot=(0,1,0;1.5708rad)
  Radius = 3
  SecondAngle = 0
FEATURE [Part::Cylinder] Cylinder110  label="円柱110"
  Angle = 360
  AttacherType = Attacher::AttachEngine3D
  FirstAngle = 0
  Height = 10
  Placement = pos=(45.6,53.35,15) rot=(0,1,0;1.5708rad)
  Radius = 3
  SecondAngle = 0
FEATURE [Part::Cylinder] Cylinder111  label="円柱111"
  Angle = 360
  AttacherType = Attacher::AttachEngine3D
  FirstAngle = 0
  Height = 10
  Placement = pos=(45.6,62,0) rot=(0,1,0;1.5708rad)
  Radius = 3
  SecondAngle = 0
FEATURE [Part::Cylinder] Cylinder113  label="円柱113"
  Angle = 360
  AttacherType = Attacher::AttachEngine3D
  FirstAngle = 0
  Height = 5
  Placement = pos=(55.6,70.66,15) rot=(0,1,0;1.5708rad)
  Radius = 1.5
  SecondAngle = 0
FEATURE [Part::Cylinder] Cylinder114  label="円柱114"
  Angle = 360
  AttacherType = Attacher::AttachEngine3D
  FirstAngle = 0
  Height = 5
  Placement = pos=(55.6,53.35,15) rot=(0,1,0;1.5708rad)
  Radius = 1.5
  SecondAngle = 0
FEATURE [Part::Cylinder] Cylinder115  label="円柱115"
  Angle = 360
  AttacherType = Attacher::AttachEngine3D
  FirstAngle = 0
  Height = 5
  Placement = pos=(55.6,62,0) rot=(0,1,0;1.5708rad)
  Radius = 1.5
  SecondAngle = 0
FEATURE [Part::Cylinder] Cylinder117  label="円柱117"
  Angle = 360
  AttacherType = Attacher::AttachEngine3D
  FirstAngle = 0
  Height = 40.5
  Placement = pos=(16.7,62,10) rot=(0,1,0;1.5708rad)
  Radius = 4
  SecondAngle = 0
FEATURE [Part::Box] Box307  label="立方体279"
  AttacherType = Attacher::AttachEngine3D
  Height = 20
  Length = 21.5
  Placement = pos=(16.7,-90,0) rot=(0,0,1;0rad)
  Width = 13
FEATURE [Part::FeaturePython] CycloidGear012  # WARN: FeaturePython — macro-defined, semantics opaque (R4)
  AttacherType = Attacher::AttachEngine3D
  Placement = pos=(-111.45,37,10) rot=(0,1,0;1.5708rad)
  angular_backlash = 0
  backlash = 0
  clearance = 0.25
  double_helix = false
  head = 0
  head_fillet = 0
  height = 4
  helix_angle = 0
  inner_diameter = 12.5
  module = 1
  num_teeth = 25
  numpoints = 20
  outer_diameter = 7.5
  pitch_diameter = 25
  root_fillet = 0
  version = 1.3.0
  expr: angular_backlash = backlash / pitch_diameter * 360 ° / pi
  expr: inner_diameter = num_teeth / 2
  expr: pitch_diameter = num_teeth * module
FEATURE [Part::FeaturePython] CycloidGear013  # WARN: FeaturePython — macro-defined, semantics opaque (R4)
  AttacherType = Attacher::AttachEngine3D
  Placement = pos=(-111.45,37,10) rot=(0,1,0;1.5708rad)
  angular_backlash = 0
  backlash = 0
  clearance = 0.25
  double_helix = false
  head = 0
  head_fillet = 0
  height = 4
  helix_angle = 0
  inner_diameter = 12.5
  module = 0.24
  num_teeth = 25
  numpoints = 20
  outer_diameter = 7.5
  pitch_diameter = 6
  root_fillet = 0
  version = 1.3.0
  expr: angular_backlash = backlash / pitch_diameter * 360 ° / pi
  expr: inner_diameter = num_teeth / 2
  expr: pitch_diameter = num_teeth * module
FEATURE [Part::Cut] Cut074  label="左上モーター側ギア"
  Base = -> CycloidGear012
  Placement = pos=(151.05,-94,0) rot=(0,0,1;0rad)
  Tool = -> CycloidGear013
FEATURE [Part::FeaturePython] CycloidGear014  # WARN: FeaturePython — macro-defined, semantics opaque (R4)
  AttacherType = Attacher::AttachEngine3D
  Placement = pos=(39.6,-82,10) rot=(0,1,0;1.5708rad)
  angular_backlash = 0
  backlash = 0
  clearance = 0.25
  double_helix = false
  head = 0
  head_fillet = 0
  height = 4
  helix_angle = 0
  inner_diameter = 12.5
  module = 1
  num_teeth = 25
  numpoints = 20
  outer_diameter = 7.5
  pitch_diameter = 25
  root_fillet = 0
  version = 1.3.0
  expr: angular_backlash = backlash / pitch_diameter * 360 ° / pi
  expr: inner_diameter = num_teeth / 2
  expr: pitch_diameter = num_teeth * module
FEATURE [Part::Cylinder] Cylinder118  label="円柱118"
  Angle = 360
  AttacherType = Attacher::AttachEngine3D
  FirstAngle = 0
  Height = 1.4
  Placement = pos=(38.2,-82,10) rot=(0,1,0;1.5708rad)
  Radius = 5
  SecondAngle = 0
FEATURE [Part::Cylinder] Cylinder119  label="円柱119"
  Angle = 360
  AttacherType = Attacher::AttachEngine3D
  FirstAngle = 0
  Height = 40.5
  Placement = pos=(16.7,-82,10) rot=(0,1,0;1.5708rad)
  Radius = 4
  SecondAngle = 0
FEATURE [Part::Cylinder] Cylinder121  label="円柱121"
  Angle = 360
  AttacherType = Attacher::AttachEngine3D
  FirstAngle = 0
  Height = 10
  Placement = pos=(45.6,-73.34,15) rot=(0,1,0;1.5708rad)
  Radius = 3
  SecondAngle = 0
FEATURE [Part::Cylinder] Cylinder122  label="円柱122"
  Angle = 360
  AttacherType = Attacher::AttachEngine3D
  FirstAngle = 0
  Height = 10
  Placement = pos=(45.6,-90.65,15) rot=(0,1,0;1.5708rad)
  Radius = 3
  SecondAngle = 0
FEATURE [Part::Cylinder] Cylinder123  label="円柱123"
  Angle = 360
  AttacherType = Attacher::AttachEngine3D
  FirstAngle = 0
  Height = 10
  Placement = pos=(45.6,-82,0) rot=(0,1,0;1.5708rad)
  Radius = 3
  SecondAngle = 0
FEATURE [Part::Cylinder] Cylinder124  label="円柱124"
  Angle = 360
  AttacherType = Attacher::AttachEngine3D
  FirstAngle = 0
  Height = 5
  Placement = pos=(55.6,-73.34,15) rot=(0,1,0;1.5708rad)
  Radius = 1.5
  SecondAngle = 0
FEATURE [Part::Cylinder] Cylinder125  label="円柱125"
  Angle = 360
  AttacherType = Attacher::AttachEngine3D
  FirstAngle = 0
  Height = 5
  Placement = pos=(55.6,-90.65,15) rot=(0,1,0;1.5708rad)
  Radius = 1.5
  SecondAngle = 0
FEATURE [Part::Cylinder] Cylinder126  label="円柱126"
  Angle = 360
  AttacherType = Attacher::AttachEngine3D
  FirstAngle = 0
  Height = 5
  Placement = pos=(55.6,-82,0) rot=(0,1,0;1.5708rad)
  Radius = 1.5
  SecondAngle = 0
FEATURE [Part::FeaturePython] Tube018  # WARN: FeaturePython — macro-defined, semantics opaque (R4)
  AttacherType = Attacher::AttachEngine3D
  Height = 2
  InnerRadius = 6
  OuterRadius = 15
  Placement = pos=(43.6,-82,10) rot=(0,1,0;1.5708rad)
FEATURE [Part::Box] Box309  label="立方体281"
  AttacherType = Attacher::AttachEngine3D
  Height = 5
  Length = 43
  Placement = pos=(8,-18,0) rot=(0,0,1;0rad)
  Width = 16
FEATURE [Part::Box] Box310  label="立方体282"
  AttacherType = Attacher::AttachEngine3D
  Height = 5
  Length = 43
  Placement = pos=(-119,-18,0) rot=(0,0,1;0rad)
  Width = 16
FEATURE [Part::Cylinder] Cylinder127  label="円柱127"
  Angle = 360
  AttacherType = Attacher::AttachEngine3D
  FirstAngle = 0
  Height = 170
  Placement = pos=(-119,28,146.3) rot=(0,1,0;1.5708rad)
  Radius = 10
  SecondAngle = 0
FEATURE [Part::Box] Box312  label="立方体284"
  AttacherType = Attacher::AttachEngine3D
  Height = 20
  Length = 21.5
  Placement = pos=(-106,57.1,0) rot=(0,0,1;0rad)
  Width = 13
FEATURE [Part::Box] Box315  label="立方体287"
  AttacherType = Attacher::AttachEngine3D
  Height = 20
  Length = 12.7
  Placement = pos=(16.7,54.1,0) rot=(0,0,1;0rad)
  Width = 3
FEATURE [Part::Cylinder] Cylinder001  label="円柱001"
  Angle = 360
  AttacherType = Attacher::AttachEngine3D
  FirstAngle = 0
  Height = 0.8
  Radius = 7.8
  SecondAngle = 0
FEATURE [Part::Cylinder] Cylinder128  label="円柱128"
  Angle = 360
  AttacherType = Attacher::AttachEngine3D
  FirstAngle = 0
  Height = 4
  Radius = 7
  SecondAngle = 0
FEATURE [Part::MultiFuse] Fusion137
  Placement = pos=(-107.4,62,10) rot=(0,-1,0;1.5708rad)
  Shapes = -> [Cylinder001,Cylinder128]
FEATURE [Part::Cut] Cut
  Base = -> CycloidGear001
  Tool = -> Fusion137
FEATURE [Part::Cylinder] Cylinder129  label="円柱129"
  Angle = 360
  AttacherType = Attacher::AttachEngine3D
  FirstAngle = 0
  Height = 0.8
  Radius = 7.8
  SecondAngle = 0
FEATURE [Part::Cylinder] Cylinder130  label="円柱130"
  Angle = 360
  AttacherType = Attacher::AttachEngine3D
  FirstAngle = 0
  Height = 4
  Radius = 7
  SecondAngle = 0
FEATURE [Part::MultiFuse] Fusion138
  Placement = pos=(-107.4,-82,10) rot=(0,-1,0;1.5708rad)
  Shapes = -> [Cylinder129,Cylinder130]
FEATURE [Part::Cut] Cut087
  Base = -> CycloidGear009
  Tool = -> Fusion138
FEATURE [Part::Cylinder] Cylinder131  label="円柱131"
  Angle = 360
  AttacherType = Attacher::AttachEngine3D
  FirstAngle = 0
  Height = 0.8
  Radius = 7.8
  SecondAngle = 0
FEATURE [Part::Cylinder] Cylinder132  label="円柱132"
  Angle = 360
  AttacherType = Attacher::AttachEngine3D
  FirstAngle = 0
  Height = 4
  Radius = 7
  SecondAngle = 0
FEATURE [Part::MultiFuse] Fusion139
  Placement = pos=(39.6,-82,10) rot=(0,1,0;1.5708rad)
  Shapes = -> [Cylinder131,Cylinder132]
FEATURE [Part::Cylinder] Cylinder133  label="円柱133"
  Angle = 360
  AttacherType = Attacher::AttachEngine3D
  FirstAngle = 0
  Height = 0.8
  Radius = 7.8
  SecondAngle = 0
FEATURE [Part::Cylinder] Cylinder134  label="円柱134"
  Angle = 360
  AttacherType = Attacher::AttachEngine3D
  FirstAngle = 0
  Height = 4
  Radius = 7
  SecondAngle = 0
FEATURE [Part::MultiFuse] Fusion140
  Placement = pos=(39.6,62,10) rot=(0,1,0;1.5708rad)
  Shapes = -> [Cylinder133,Cylinder134]
FEATURE [Part::Cut] Cut088
  Base = -> CycloidGear014
  Tool = -> Fusion139
FEATURE [Part::Cut] Cut089
  Base = -> CycloidGear004
  Tool = -> Fusion140
FEATURE [Part::Cylinder] Cylinder135  label="円柱135"
  Angle = 360
  AttacherType = Attacher::AttachEngine3D
  FirstAngle = 0
  Height = 47.8
  Placement = pos=(9.4,62,10) rot=(0,1,0;1.5708rad)
  Radius = 2
  SecondAngle = 0
FEATURE [Part::Cylinder] Cylinder136  label="円柱136"
  Angle = 360
  AttacherType = Attacher::AttachEngine3D
  FirstAngle = 0
  Height = 47.8
  Placement = pos=(9.4,-82,10) rot=(0,1,0;1.5708rad)
  Radius = 2
  SecondAngle = 0
FEATURE [Part::MultiFuse] Fusion141
  Shapes = -> [Cylinder108,Cylinder117]
FEATURE [Part::Cut] Cut092  label="左下車軸"
  Base = -> Fusion141
  Placement = pos=(-4,-10,0) rot=(0,0,1;0rad)
  Tool = -> Cylinder135
FEATURE [Part::Cylinder] Cylinder137  label="円柱137"
  Angle = 360
  AttacherType = Attacher::AttachEngine3D
  FirstAngle = 0
  Height = 47.8
  Placement = pos=(9.4,62,10) rot=(0,1,0;1.5708rad)
  Radius = 4
  SecondAngle = 0
FEATURE [Part::Cut] Cut093
  Base = -> Box242
  Placement = pos=(-3.3,-10,0) rot=(0,0,1;0rad)
  Tool = -> Cylinder137
FEATURE [Part::Cylinder] Cylinder138  label="円柱138"
  Angle = 360
  AttacherType = Attacher::AttachEngine3D
  FirstAngle = 0
  Height = 47.8
  Placement = pos=(-125,62,10) rot=(0,1,0;1.5708rad)
  Radius = 2
  SecondAngle = 0
FEATURE [Part::Cylinder] Cylinder139  label="円柱139"
  Angle = 360
  AttacherType = Attacher::AttachEngine3D
  FirstAngle = 0
  Height = 47.8
  Placement = pos=(-125,62,10) rot=(0,1,0;1.5708rad)
  Radius = 4
  SecondAngle = 0
FEATURE [Part::MultiFuse] Fusion142
  Shapes = -> [Cylinder072,Cylinder091]
FEATURE [Part::Cut] Cut095  label="右下車軸"
  Base = -> Fusion142
  Placement = pos=(4,-10,0) rot=(0,0,1;0rad)
  Tool = -> Cylinder138
FEATURE [Part::MultiFuse] Fusion143
  Shapes = -> [Cylinder119,Cylinder118]
FEATURE [Part::Cut] Cut096  label="右上車軸"
  Base = -> Fusion143
  Placement = pos=(-4,10,0) rot=(0,0,1;0rad)
  Tool = -> Cylinder136
FEATURE [Part::Cylinder] Cylinder140  label="円柱140"
  Angle = 360
  AttacherType = Attacher::AttachEngine3D
  FirstAngle = 0
  Height = 47.8
  Placement = pos=(9.4,-82,10) rot=(0,1,0;1.5708rad)
  Radius = 4
  SecondAngle = 0
FEATURE [Part::Cylinder] Cylinder142  label="円柱142"
  Angle = 360
  AttacherType = Attacher::AttachEngine3D
  FirstAngle = 0
  Height = 5
  Placement = pos=(-128.4,-90.65,15) rot=(0,1,0;1.5708rad)
  Radius = 1.5
  SecondAngle = 0
FEATURE [Part::Cylinder] Cylinder143  label="円柱143"
  Angle = 360
  AttacherType = Attacher::AttachEngine3D
  FirstAngle = 0
  Height = 5
  Placement = pos=(-128.4,-82,0) rot=(0,1,0;1.5708rad)
  Radius = 1.5
  SecondAngle = 0
FEATURE [Part::Cylinder] Cylinder144  label="円柱144"
  Angle = 360
  AttacherType = Attacher::AttachEngine3D
  FirstAngle = 0
  Height = 5
  Placement = pos=(-128.4,-73.34,15) rot=(0,1,0;1.5708rad)
  Radius = 1.5
  SecondAngle = 0
FEATURE [Part::Cylinder] Cylinder145  label="円柱145"
  Angle = 360
  AttacherType = Attacher::AttachEngine3D
  FirstAngle = 0
  Height = 47.8
  Placement = pos=(-125,-82,10) rot=(0,1,0;1.5708rad)
  Radius = 2
  SecondAngle = 0
FEATURE [Part::MultiFuse] Fusion144
  Shapes = -> [Cylinder093,Cylinder106]
FEATURE [Part::Cut] Cut098  label="左上車軸"
  Base = -> Fusion144
  Placement = pos=(4,10,0) rot=(0,0,1;0rad)
  Tool = -> Cylinder145
FEATURE [Part::Cylinder] Cylinder146  label="円柱146"
  Angle = 360
  AttacherType = Attacher::AttachEngine3D
  FirstAngle = 0
  Height = 47.8
  Placement = pos=(-125,-82,10) rot=(0,1,0;1.5708rad)
  Radius = 4
  SecondAngle = 0
FEATURE [Part::MultiFuse] Fusion145  label="右上車軸側ギア"
  Placement = pos=(4,10,0) rot=(0,0,1;0rad)
  Shapes = -> [Cylinder142,Cylinder089,Cylinder143,Cylinder102,Cylinder144,Cylinder101,Tube014,Cut087]
FEATURE [Part::MultiFuse] Fusion146  label="左上車軸側ギア"
  Placement = pos=(-4,10,0) rot=(0,0,1;0rad)
  Shapes = -> [Cylinder124,Cylinder121,Cylinder122,Cylinder125,Cylinder126,Cylinder123,Tube018,Cut088]
FEATURE [Part::MultiFuse] Fusion147  label="左下車軸側ギア"
  Placement = pos=(-4,-10,0) rot=(0,0,1;0rad)
  Shapes = -> [Cylinder109,Cylinder113,Cylinder111,Cylinder115,Cylinder110,Cylinder114,Tube017,Cut089]
FEATURE [Part::MultiFuse] Fusion148  label="右下車軸側ギア"
  Placement = pos=(4,-10,0) rot=(0,0,1;0rad)
  Shapes = -> [Cylinder085,Cylinder100,Cylinder087,Cylinder090,Cylinder086,Cylinder088,Tube,Cut]
FEATURE [Part::Cylinder] Cylinder147  label="円柱147"
  Angle = 360
  AttacherType = Attacher::AttachEngine3D
  FirstAngle = 0
  Height = 20
  Placement = pos=(9.4,51.9,5) rot=(0,1,0;1.5708rad)
  Radius = 2
  SecondAngle = 0
FEATURE [Part::Cylinder] Cylinder148  label="円柱148"
  Angle = 360
  AttacherType = Attacher::AttachEngine3D
  FirstAngle = 0
  Height = 20
  Placement = pos=(9.4,51.9,15) rot=(0,1,0;1.5708rad)
  Radius = 2
  SecondAngle = 0
FEATURE [Part::Cylinder] Cylinder153  label="円柱153"
  Angle = 360
  AttacherType = Attacher::AttachEngine3D
  FirstAngle = 0
  Height = 20
  Placement = pos=(9.4,-71.8,15) rot=(0,1,0;1.5708rad)
  Radius = 2
  SecondAngle = 0
FEATURE [Part::Cylinder] Cylinder154  label="円柱154"
  Angle = 360
  AttacherType = Attacher::AttachEngine3D
  FirstAngle = 0
  Height = 20
  Placement = pos=(9.4,-71.8,5) rot=(0,1,0;1.5708rad)
  Radius = 2
  SecondAngle = 0
FEATURE [Part::Cylinder] Cylinder155  label="円柱155"
  Angle = 360
  AttacherType = Attacher::AttachEngine3D
  FirstAngle = 0
  Height = 20
  Placement = pos=(-97.2,51.9,5) rot=(0,1,0;1.5708rad)
  Radius = 2
  SecondAngle = 0
FEATURE [Part::Cylinder] Cylinder161  label="円柱161"
  Angle = 360
  AttacherType = Attacher::AttachEngine3D
  FirstAngle = 0
  Height = 20
  Placement = pos=(-97.2,-71.8,15) rot=(0,1,0;1.5708rad)
  Radius = 2
  SecondAngle = 0
FEATURE [Part::Cylinder] Cylinder162  label="円柱162"
  Angle = 360
  AttacherType = Attacher::AttachEngine3D
  FirstAngle = 0
  Height = 20
  Placement = pos=(-97.2,-71.8,5) rot=(0,1,0;1.5708rad)
  Radius = 2
  SecondAngle = 0
FEATURE [Part::Cylinder] Cylinder163  label="円柱163"
  Angle = 360
  AttacherType = Attacher::AttachEngine3D
  FirstAngle = 0
  Height = 20
  Placement = pos=(9.4,51.9,5) rot=(0,1,0;1.5708rad)
  Radius = 2
  SecondAngle = 0
FEATURE [Part::Cylinder] Cylinder164  label="円柱164"
  Angle = 360
  AttacherType = Attacher::AttachEngine3D
  FirstAngle = 0
  Height = 20
  Placement = pos=(9.4,51.9,15) rot=(0,1,0;1.5708rad)
  Radius = 2
  SecondAngle = 0
FEATURE [Part::Cylinder] Cylinder165  label="円柱165"
  Angle = 360
  AttacherType = Attacher::AttachEngine3D
  FirstAngle = 0
  Height = 20
  Placement = pos=(9.4,2.2,15) rot=(0,1,0;1.5708rad)
  Radius = 2
  SecondAngle = 0
FEATURE [Part::Cylinder] Cylinder166  label="円柱166"
  Angle = 360
  AttacherType = Attacher::AttachEngine3D
  FirstAngle = 0
  Height = 20
  Placement = pos=(9.4,2.2,5) rot=(0,1,0;1.5708rad)
  Radius = 2
  SecondAngle = 0
FEATURE [Part::Cylinder] Cylinder167  label="円柱167"
  Angle = 360
  AttacherType = Attacher::AttachEngine3D
  FirstAngle = 0
  Height = 20
  Placement = pos=(9.4,-22.1,5) rot=(0,1,0;1.5708rad)
  Radius = 2
  SecondAngle = 0
FEATURE [Part::Cylinder] Cylinder168  label="円柱168"
  Angle = 360
  AttacherType = Attacher::AttachEngine3D
  FirstAngle = 0
  Height = 20
  Placement = pos=(9.4,-22.1,15) rot=(0,1,0;1.5708rad)
  Radius = 2
  SecondAngle = 0
FEATURE [Part::Cylinder] Cylinder169  label="円柱169"
  Angle = 360
  AttacherType = Attacher::AttachEngine3D
  FirstAngle = 0
  Height = 20
  Placement = pos=(9.4,-71.8,15) rot=(0,1,0;1.5708rad)
  Radius = 2
  SecondAngle = 0
FEATURE [Part::Cylinder] Cylinder170  label="円柱170"
  Angle = 360
  AttacherType = Attacher::AttachEngine3D
  FirstAngle = 0
  Height = 20
  Placement = pos=(9.4,-71.8,5) rot=(0,1,0;1.5708rad)
  Radius = 2
  SecondAngle = 0
FEATURE [Part::Cylinder] Cylinder171  label="円柱171"
  Angle = 360
  AttacherType = Attacher::AttachEngine3D
  FirstAngle = 0
  Height = 20
  Placement = pos=(-97.2,51.9,5) rot=(0,1,0;1.5708rad)
  Radius = 2
  SecondAngle = 0
FEATURE [Part::Cylinder] Cylinder172  label="円柱172"
  Angle = 360
  AttacherType = Attacher::AttachEngine3D
  FirstAngle = 0
  Height = 20
  Placement = pos=(-97.2,51.9,15) rot=(0,1,0;1.5708rad)
  Radius = 2
  SecondAngle = 0
FEATURE [Part::Cylinder] Cylinder173  label="円柱173"
  Angle = 360
  AttacherType = Attacher::AttachEngine3D
  FirstAngle = 0
  Height = 20
  Placement = pos=(-97.2,2.2,15) rot=(0,1,0;1.5708rad)
  Radius = 2
  SecondAngle = 0
FEATURE [Part::Cylinder] Cylinder174  label="円柱174"
  Angle = 360
  AttacherType = Attacher::AttachEngine3D
  FirstAngle = 0
  Height = 20
  Placement = pos=(-97.2,2.2,5) rot=(0,1,0;1.5708rad)
  Radius = 2
  SecondAngle = 0
FEATURE [Part::Cylinder] Cylinder175  label="円柱175"
  Angle = 360
  AttacherType = Attacher::AttachEngine3D
  FirstAngle = 0
  Height = 20
  Placement = pos=(-97.2,-22.1,5) rot=(0,1,0;1.5708rad)
  Radius = 2
  SecondAngle = 0
FEATURE [Part::Cylinder] Cylinder176  label="円柱176"
  Angle = 360
  AttacherType = Attacher::AttachEngine3D
  FirstAngle = 0
  Height = 20
  Placement = pos=(-97.2,-22.1,15) rot=(0,1,0;1.5708rad)
  Radius = 2
  SecondAngle = 0
FEATURE [Part::Cylinder] Cylinder177  label="円柱177"
  Angle = 360
  AttacherType = Attacher::AttachEngine3D
  FirstAngle = 0
  Height = 20
  Placement = pos=(-97.2,-71.8,15) rot=(0,1,0;1.5708rad)
  Radius = 2
  SecondAngle = 0
FEATURE [Part::Cylinder] Cylinder178  label="円柱178"
  Angle = 360
  AttacherType = Attacher::AttachEngine3D
  FirstAngle = 0
  Height = 20
  Placement = pos=(-97.2,-71.8,5) rot=(0,1,0;1.5708rad)
  Radius = 2
  SecondAngle = 0
FEATURE [Part::Cut] Cut116
  Base = -> Fusion087
  Tool = -> Cylinder164
FEATURE [Part::Cut] Cut117
  Base = -> Cut116
  Tool = -> Cylinder163
FEATURE [Part::Cut] Cut118
  Base = -> Cut117
  Tool = -> Cylinder165
FEATURE [Part::Cut] Cut119  label="左下モーターー"
  Base = -> Cut118
  Placement = pos=(-4,-10,0) rot=(0,0,1;0rad)
  Tool = -> Cylinder166
FEATURE [Part::Cut] Cut120
  Base = -> Fusion086
  Tool = -> Cylinder168
FEATURE [Part::Cut] Cut121
  Base = -> Cut120
  Tool = -> Cylinder167
FEATURE [Part::Cut] Cut122
  Base = -> Cut121
  Tool = -> Cylinder169
FEATURE [Part::Cut] Cut123  label="左上モーター"
  Base = -> Cut122
  Placement = pos=(-4,10,0) rot=(0,0,1;0rad)
  Tool = -> Cylinder170
FEATURE [Part::Cut] Cut124
  Base = -> Fusion085
  Tool = -> Cylinder172
FEATURE [Part::Cut] Cut125
  Base = -> Cut124
  Tool = -> Cylinder171
FEATURE [Part::Cut] Cut126
  Base = -> Cut125
  Tool = -> Cylinder173
FEATURE [Part::Cut] Cut127  label="右下モーター"
  Base = -> Cut126
  Placement = pos=(4,-10,0) rot=(0,0,1;0rad)
  Tool = -> Cylinder174
FEATURE [Part::Cut] Cut128
  Base = -> Fusion084
  Tool = -> Cylinder176
FEATURE [Part::Cut] Cut129
  Base = -> Cut128
  Tool = -> Cylinder175
FEATURE [Part::Cut] Cut130
  Base = -> Cut129
  Tool = -> Cylinder177
FEATURE [Part::Cut] Cut131  label="右上モーター"
  Base = -> Cut130
  Placement = pos=(4,10,0) rot=(0,0,1;0rad)
  Tool = -> Cylinder178
FEATURE [Part::Part2DObjectPython] Wire004  # Draft 2D object (typed FeaturePython)
  Area = 2400
  ChamferSize = 0
  Closed = true
  End = (40,150,0)
  FilletRadius = 0
  Length = 342.483
  MakeFace = true
  Points = (4) [(0,0,0),(16,0,0),(56,150,0),(40,150,0)]
  Start = (0,0,0)
  Subdivisions = 0
FEATURE [Part::Extrusion] Extrude009
  Base = -> Wire004
  Dir = (0,0,1)
  DirMode = 2
  FaceMakerClass = Part::FaceMakerBullseye
  FaceMakerMode = 3
  LengthFwd = 10
  LengthRev = 0
  Solid = false
  Symmetric = false
FEATURE [Part::Fillet] Fillet002
  Base = -> Extrude009
  EdgeLinks = -> Extrude009 [Edge5,Edge8]
  Edges = 2 edges r=7.72: [Edge5,Edge8]
  Placement = pos=(41,-18,5) rot=(0.57735,0.57735,0.57735;2.0944rad)
FEATURE [Part::Part2DObjectPython] Wire005  # Draft 2D object (typed FeaturePython)
  Area = 2400
  ChamferSize = 0
  Closed = true
  End = (40,150,0)
  FilletRadius = 0
  Length = 342.483
  MakeFace = true
  Points = (4) [(0,0,0),(16,0,0),(56,150,0),(40,150,0)]
  Start = (0,0,0)
  Subdivisions = 0
FEATURE [Part::Extrusion] Extrude010
  Base = -> Wire005
  Dir = (0,0,1)
  DirMode = 2
  FaceMakerClass = Part::FaceMakerBullseye
  FaceMakerMode = 3
  LengthFwd = 10
  LengthRev = 0
  Solid = false
  Symmetric = false
FEATURE [Part::Fillet] Fillet003
  Base = -> Extrude010
  EdgeLinks = -> Extrude010 [Edge5,Edge8]
  Edges = 2 edges r=7.72: [Edge5,Edge8]
  Placement = pos=(-119,-18,5) rot=(0.57735,0.57735,0.57735;2.0944rad)
FEATURE [Part::Cylinder] Cylinder179  label="円柱179"
  Angle = 360
  AttacherType = Attacher::AttachEngine3D
  FirstAngle = 0
  Height = 30
  Placement = pos=(-71.6,-105.8,73) rot=(0,1,0;1.5708rad)
  Radius = 2
  SecondAngle = 0
FEATURE [Part::Cylinder] Cylinder180  label="円柱180"
  Angle = 360
  AttacherType = Attacher::AttachEngine3D
  FirstAngle = 0
  Height = 33
  Placement = pos=(-74.6,-105.8,63) rot=(0,1,0;1.5708rad)
  Radius = 2
  SecondAngle = 0
FEATURE [Part::Cylinder] Cylinder181  label="円柱181"
  Angle = 360
  AttacherType = Attacher::AttachEngine3D
  FirstAngle = 0
  Height = 30
  Placement = pos=(-71.6,-56.2,73) rot=(0,1,0;1.5708rad)
  Radius = 2
  SecondAngle = 0
FEATURE [Part::Cylinder] Cylinder182  label="円柱182"
  Angle = 360
  AttacherType = Attacher::AttachEngine3D
  FirstAngle = 0
  Height = 33
  Placement = pos=(-74.6,-56.2,63) rot=(0,1,0;1.5708rad)
  Radius = 2
  SecondAngle = 0
FEATURE [Part::Cylinder] Cylinder183  label="円柱183"
  Angle = 360
  AttacherType = Attacher::AttachEngine3D
  FirstAngle = 0
  Height = 30
  Placement = pos=(-71.6,-105.8,73) rot=(0,1,0;1.5708rad)
  Radius = 2
  SecondAngle = 0
FEATURE [Part::Cylinder] Cylinder184  label="円柱184"
  Angle = 360
  AttacherType = Attacher::AttachEngine3D
  FirstAngle = 0
  Height = 33
  Placement = pos=(-74.6,-105.8,63) rot=(0,1,0;1.5708rad)
  Radius = 2
  SecondAngle = 0
FEATURE [Part::Cylinder] Cylinder185  label="円柱185"
  Angle = 360
  AttacherType = Attacher::AttachEngine3D
  FirstAngle = 0
  Height = 30
  Placement = pos=(-71.6,-56.2,73) rot=(0,1,0;1.5708rad)
  Radius = 2
  SecondAngle = 0
FEATURE [Part::Cylinder] Cylinder186  label="円柱186"
  Angle = 360
  AttacherType = Attacher::AttachEngine3D
  FirstAngle = 0
  Height = 33
  Placement = pos=(-74.6,-56.2,63) rot=(0,1,0;1.5708rad)
  Radius = 2
  SecondAngle = 0
FEATURE [Part::Cut] Cut140
  Base = -> Fusion121
  Tool = -> Cylinder183
FEATURE [Part::Cut] Cut141
  Base = -> Cut140
  Tool = -> Cylinder184
FEATURE [Part::Cut] Cut142
  Base = -> Cut141
  Tool = -> Cylinder185
FEATURE [Part::Cut] Cut143  label="レスキューアームモータ　"
  Base = -> Cut142
  Placement = pos=(4.7,2,4) rot=(0,0,1;0rad)
  Tool = -> Cylinder186
FEATURE [Part::MultiFuse] Fusion
  Shapes = -> [Box097,Box098]
FEATURE [Part::Cylinder] Cylinder187  label="円柱187"
  Angle = 360
  AttacherType = Attacher::AttachEngine3D
  FirstAngle = 0
  Height = 13
  Placement = pos=(-55,-69,-5) rot=(0,0,1;0rad)
  Radius = 2
  SecondAngle = 0
FEATURE [Part::Cylinder] Cylinder188  label="円柱188"
  Angle = 360
  AttacherType = Attacher::AttachEngine3D
  FirstAngle = 0
  Height = 13
  Placement = pos=(-12,-69,-5) rot=(0,0,1;0rad)
  Radius = 2
  SecondAngle = 0
FEATURE [Part::Cylinder] Cylinder189  label="円柱189"
  Angle = 360
  AttacherType = Attacher::AttachEngine3D
  FirstAngle = 0
  Height = 20
  Placement = pos=(-53,-88,43) rot=(1,0,0;1.5708rad)
  Radius = 2
  SecondAngle = 0
FEATURE [Part::Cylinder] Cylinder190  label="円柱190"
  Angle = 360
  AttacherType = Attacher::AttachEngine3D
  FirstAngle = 0
  Height = 20
  Placement = pos=(-16,-88,43) rot=(1,0,0;1.5708rad)
  Radius = 2
  SecondAngle = 0
FEATURE [Part::Box] Box321  label="立方体293"
  AttacherType = Attacher::AttachEngine3D
  Height = 25
  Length = 23
  Placement = pos=(-46,-93,16) rot=(0,0,1;0rad)
  Width = 5
FEATURE [Part::Cut] Cut144
  Base = -> Fusion
  Placement = pos=(0,-40,96) rot=(1,0,0;1.5708rad)
  Tool = -> Box321
FEATURE [Part::Cylinder] Cylinder191  label="円柱191"
  Angle = 360
  AttacherType = Attacher::AttachEngine3D
  FirstAngle = 0
  Height = 13
  Placement = pos=(-55,-69,-5) rot=(0,0,1;0rad)
  Radius = 2
  SecondAngle = 0
FEATURE [Part::Cylinder] Cylinder192  label="円柱192"
  Angle = 360
  AttacherType = Attacher::AttachEngine3D
  FirstAngle = 0
  Height = 13
  Placement = pos=(-12,-69,-5) rot=(0,0,1;0rad)
  Radius = 2
  SecondAngle = 0
FEATURE [Part::Cut] Cut147
  Base = -> Cut144
  Tool = -> Cylinder187
FEATURE [Part::Cut] Cut148  label="ライントレースカメラふた　"
  Base = -> Cut147
  Placement = pos=(0,8,42) rot=(0,0,1;0rad)
  Tool = -> Cylinder188
FEATURE [Part::Box] Box324  label="立方体296"
  AttacherType = Attacher::AttachEngine3D
  Height = 3
  Length = 3
  Placement = pos=(-90,-22,37) rot=(0,0,1;0rad)
  Width = 68
FEATURE [Part::Box] Box325  label="立方体297"
  AttacherType = Attacher::AttachEngine3D
  Height = 13
  Length = 12
  Placement = pos=(-85,-32,34) rot=(0,0,1;0rad)
  Width = 10
FEATURE [Part::Cylinder] Cylinder195  label="円柱195"
  Angle = 360
  AttacherType = Attacher::AttachEngine3D
  FirstAngle = 0
  Height = 19
  Placement = pos=(-101,-27,32) rot=(0,0,1;0rad)
  Radius = 2
  SecondAngle = 0
FEATURE [Part::Cylinder] Cylinder196  label="円柱196"
  Angle = 360
  AttacherType = Attacher::AttachEngine3D
  FirstAngle = 0
  Height = 20
  Placement = pos=(-57,-27,32) rot=(0,0,1;0rad)
  Radius = 2
  SecondAngle = 0
FEATURE [Part::Cylinder] Cylinder197  label="円柱197"
  Angle = 360
  AttacherType = Attacher::AttachEngine3D
  FirstAngle = 0
  Height = 20
  Placement = pos=(-101,71,32) rot=(0,0,1;0rad)
  Radius = 2
  SecondAngle = 0
FEATURE [Part::Cylinder] Cylinder198  label="円柱198"
  Angle = 360
  AttacherType = Attacher::AttachEngine3D
  FirstAngle = 0
  Height = 20
  Placement = pos=(-57,71,32) rot=(0,0,1;0rad)
  Radius = 2
  SecondAngle = 0
FEATURE [Part::Cylinder] Cylinder199  label="円柱199"
  Angle = 360
  AttacherType = Attacher::AttachEngine3D
  FirstAngle = 0
  Height = 20
  Placement = pos=(-101,-27,32) rot=(0,0,1;0rad)
  Radius = 2
  SecondAngle = 0
FEATURE [Part::Cylinder] Cylinder200  label="円柱200"
  Angle = 360
  AttacherType = Attacher::AttachEngine3D
  FirstAngle = 0
  Height = 19
  Placement = pos=(-57,-27,32) rot=(0,0,1;0rad)
  Radius = 2
  SecondAngle = 0
FEATURE [Part::Cylinder] Cylinder201  label="円柱201"
  Angle = 360
  AttacherType = Attacher::AttachEngine3D
  FirstAngle = 0
  Height = 19
  Placement = pos=(-101,71,32) rot=(0,0,1;0rad)
  Radius = 2
  SecondAngle = 0
FEATURE [Part::Cylinder] Cylinder202  label="円柱202"
  Angle = 360
  AttacherType = Attacher::AttachEngine3D
  FirstAngle = 0
  Height = 19
  Placement = pos=(-57,71,32) rot=(0,0,1;0rad)
  Radius = 2
  SecondAngle = 0
FEATURE [Part::Box] Box327  label="立方体299"
  AttacherType = Attacher::AttachEngine3D
  Height = 20
  Length = 10
  Placement = pos=(28,-32,37) rot=(0,0,1;0rad)
  Width = 10
FEATURE [Part::Box] Box328  label="立方体300"
  AttacherType = Attacher::AttachEngine3D
  Height = 20
  Length = 10
  Placement = pos=(-52,-32,37) rot=(0,0,1;0rad)
  Width = 10
FEATURE [Part::Box] Box329  label="立方体301"
  AttacherType = Attacher::AttachEngine3D
  Height = 20
  Length = 10
  Placement = pos=(28,58,37) rot=(0,0,1;0rad)
  Width = 10
FEATURE [Part::Box] Box330  label="立方体302"
  AttacherType = Attacher::AttachEngine3D
  Height = 20
  Length = 10
  Placement = pos=(-52,58,37) rot=(0,0,1;0rad)
  Width = 10
FEATURE [Part::Cylinder] Cylinder203  label="円柱203"
  Angle = 360
  AttacherType = Attacher::AttachEngine3D
  FirstAngle = 0
  Height = 13
  Placement = pos=(33,-35,32) rot=(0,0,1;0rad)
  Radius = 2
  SecondAngle = 0
FEATURE [Part::Cylinder] Cylinder204  label="円柱204"
  Angle = 360
  AttacherType = Attacher::AttachEngine3D
  FirstAngle = 0
  Height = 13
  Placement = pos=(33,55,32) rot=(0,0,1;0rad)
  Radius = 2
  SecondAngle = 0
FEATURE [Part::Cylinder] Cylinder205  label="円柱205"
  Angle = 360
  AttacherType = Attacher::AttachEngine3D
  FirstAngle = 0
  Height = 13
  Placement = pos=(-47,55,32) rot=(0,0,1;0rad)
  Radius = 2
  SecondAngle = 0
FEATURE [Part::Cylinder] Cylinder206  label="円柱206"
  Angle = 360
  AttacherType = Attacher::AttachEngine3D
  FirstAngle = 0
  Height = 13
  Placement = pos=(-47,-35,32) rot=(0,0,1;0rad)
  Radius = 2
  SecondAngle = 0
FEATURE [Part::Cylinder] Cylinder207  label="円柱207"
  Angle = 360
  AttacherType = Attacher::AttachEngine3D
  FirstAngle = 0
  Height = 25
  Placement = pos=(33,-27,32) rot=(0,0,1;0rad)
  Radius = 2
  SecondAngle = 0
FEATURE [Part::Cylinder] Cylinder208  label="円柱208"
  Angle = 360
  AttacherType = Attacher::AttachEngine3D
  FirstAngle = 0
  Height = 25
  Placement = pos=(33,63,32) rot=(0,0,1;0rad)
  Radius = 2
  SecondAngle = 0
FEATURE [Part::Cylinder] Cylinder209  label="円柱209"
  Angle = 360
  AttacherType = Attacher::AttachEngine3D
  FirstAngle = 0
  Height = 25
  Placement = pos=(-47,63,32) rot=(0,0,1;0rad)
  Radius = 2
  SecondAngle = 0
FEATURE [Part::Cylinder] Cylinder210  label="円柱210"
  Angle = 360
  AttacherType = Attacher::AttachEngine3D
  FirstAngle = 0
  Height = 25
  Placement = pos=(-47,-27,32) rot=(0,0,1;0rad)
  Radius = 2
  SecondAngle = 0
FEATURE [Part::Cut] Cut168
  Base = -> Box259
  Tool = -> Cylinder206
FEATURE [Part::Cut] Cut169
  Base = -> Cut168
  Tool = -> Cylinder203
FEATURE [Part::Cut] Cut170
  Base = -> Cut169
  Tool = -> Cylinder205
FEATURE [Part::Cut] Cut171  label="基盤"
  Base = -> Cut170
  Placement = pos=(0,16,15) rot=(0,0,1;0rad)
  Tool = -> Cylinder204
FEATURE [Part::Cylinder] Cylinder212  label="円柱212"
  Angle = 360
  AttacherType = Attacher::AttachEngine3D
  FirstAngle = 0
  Height = 47
  Placement = pos=(7,-98,-5) rot=(0,0,1;0rad)
  Radius = 2
  SecondAngle = 0
FEATURE [Part::Cylinder] Cylinder213  label="円柱213"
  Angle = 360
  AttacherType = Attacher::AttachEngine3D
  FirstAngle = 0
  Height = 37
  Placement = pos=(15.2,-98,0) rot=(0,0,1;0rad)
  Radius = 2
  SecondAngle = 0
FEATURE [Part::Cylinder] Cylinder214  label="円柱214"
  Angle = 360
  AttacherType = Attacher::AttachEngine3D
  FirstAngle = 0
  Height = 42
  Placement = pos=(-83,-98,-5) rot=(0,0,1;0rad)
  Radius = 2
  SecondAngle = 0
FEATURE [Part::Cut] Cut182
  Base = -> Cylinder016
  Placement = pos=(8,0,0) rot=(0,0,1;0rad)
  Tool = -> Cylinder214
FEATURE [Part::Cut] Cut183
  Base = -> Box310
  Tool = -> Cylinder034
FEATURE [Part::Cut] Cut187
  Base = -> Box309
  Tool = -> Cylinder033
FEATURE [Part::Cylinder] Cylinder225  label="円柱225"
  Angle = 360
  AttacherType = Attacher::AttachEngine3D
  FirstAngle = 0
  Height = 32
  Placement = pos=(-68,82,0) rot=(0,0,1;0rad)
  Radius = 4
  SecondAngle = 0
FEATURE [Part::Cylinder] Cylinder227  label="円柱227"
  Angle = 360
  AttacherType = Attacher::AttachEngine3D
  FirstAngle = 0
  Height = 42
  Placement = pos=(-81.9,72,-5) rot=(0,0,1;0rad)
  Radius = 2
  SecondAngle = 0
FEATURE [Part::Cut] Cut191
  Base = -> Cylinder225
  Placement = pos=(-13.9,-10,0) rot=(0,0,1;0rad)
  Tool = -> Cylinder012
FEATURE [Part::Cylinder] Cylinder229  label="円柱229"
  Angle = 360
  AttacherType = Attacher::AttachEngine3D
  FirstAngle = 0
  Height = 42
  Placement = pos=(14.1,72,-5) rot=(0,0,1;0rad)
  Radius = 2
  SecondAngle = 0
FEATURE [Part::Cylinder] Cylinder230  label="円柱230"
  Angle = 360
  AttacherType = Attacher::AttachEngine3D
  FirstAngle = 0
  Height = 42
  Placement = pos=(0,82,-5) rot=(0,0,1;0rad)
  Radius = 2
  SecondAngle = 0
FEATURE [Part::Cut] Cut196
  Base = -> Cylinder007
  Placement = pos=(14.1,-10,0) rot=(0,0,1;0rad)
  Tool = -> Cylinder230
FEATURE [Part::Cylinder] Cylinder236  label="円柱236"
  Angle = 360
  AttacherType = Attacher::AttachEngine3D
  FirstAngle = 0
  Height = 42
  Placement = pos=(-85,-10,-5) rot=(0,0,1;0rad)
  Radius = 2
  SecondAngle = 0
FEATURE [Part::Cylinder] Cylinder237  label="円柱237"
  Angle = 360
  AttacherType = Attacher::AttachEngine3D
  FirstAngle = 0
  Height = 42
  Placement = pos=(17.2,-10,-5) rot=(0,0,1;0rad)
  Radius = 2
  SecondAngle = 0
FEATURE [Part::Cut] Cut202
  Base = -> Cut183
  Tool = -> Cylinder236
FEATURE [Part::Cut] Cut203
  Base = -> Cut187
  Tool = -> Cylinder237
FEATURE [Part::MultiFuse] Fusion167
  Shapes = -> [Fillet002,Cylinder127,Fillet003]
FEATURE [Part::MultiFuse] Fusion169  label="持ち手"
  Placement = pos=(0,0,20.1) rot=(0,0,1;0rad)
  Shapes = -> [Cut202,Fusion167,Cut203]
FEATURE [Part::Cylinder] Cylinder264  label="円柱264"
  Angle = 360
  AttacherType = Attacher::AttachEngine3D
  FirstAngle = 0
  Height = 12
  Placement = pos=(1.4,70,0) rot=(0,0,1;0rad)
  Radius = 2
  SecondAngle = 0
FEATURE [Part::Cylinder] Cylinder265  label="円柱265"
  Angle = 360
  AttacherType = Attacher::AttachEngine3D
  FirstAngle = 0
  Height = 12
  Placement = pos=(-70.2,70,0) rot=(0,0,1;0rad)
  Radius = 2
  SecondAngle = 0
FEATURE [Part::Box] Box343  label="立方体315"
  AttacherType = Attacher::AttachEngine3D
  Height = 25
  Length = 54
  Placement = pos=(-60.9,-98,22) rot=(0,0,1;0rad)
  Width = 5
FEATURE [Part::Box] Box016  label="機体底面"
  AttacherType = Attacher::AttachEngine3D
  Height = 5
  Length = 136.2
  Placement = pos=(-102,-108,-5) rot=(0,0,1;0rad)
  Width = 184
FEATURE [Part::Cylinder] Cylinder156  label="円柱156"
  Angle = 360
  AttacherType = Attacher::AttachEngine3D
  FirstAngle = 0
  Height = 20
  Placement = pos=(-97.2,51.9,15) rot=(0,1,0;1.5708rad)
  Radius = 2
  SecondAngle = 0
FEATURE [Part::Box] Box344  label="立方体316"
  AttacherType = Attacher::AttachEngine3D
  Height = 20
  Length = 10
  Placement = pos=(16.7,-74,0) rot=(0,0,1;0rad)
  Width = 7
FEATURE [Part::Box] Box345  label="立方体317"
  AttacherType = Attacher::AttachEngine3D
  Height = 20
  Length = 10
  Placement = pos=(-94.5,47.1,0) rot=(0,0,1;0rad)
  Width = 7
FEATURE [Part::Box] Box346  label="立方体318"
  AttacherType = Attacher::AttachEngine3D
  Height = 20
  Length = 10
  Placement = pos=(-94.5,-74,0) rot=(0,0,1;0rad)
  Width = 7
FEATURE [Part::Box] Box347  label="立方体319"
  AttacherType = Attacher::AttachEngine3D
  Height = 20
  Length = 12.7
  Placement = pos=(16.7,-77,0) rot=(0,0,1;0rad)
  Width = 3
FEATURE [Part::Box] Box348  label="立方体320"
  AttacherType = Attacher::AttachEngine3D
  Height = 20
  Length = 12.7
  Placement = pos=(-97.2,54.1,0) rot=(0,0,1;0rad)
  Width = 3
FEATURE [Part::Box] Box349  label="立方体321"
  AttacherType = Attacher::AttachEngine3D
  Height = 20
  Length = 12.7
  Placement = pos=(-97.2,-77,0) rot=(0,0,1;0rad)
  Width = 3
FEATURE [Part::Box] Box351  label="立方体323"
  AttacherType = Attacher::AttachEngine3D
  Height = 20.1
  Length = 12
  Placement = pos=(10.7,-16.9,0) rot=(0,0,1;0rad)
  Width = 13.9
FEATURE [Part::MultiFuse] Fusion184
  Shapes = -> [Box344,Box347]
FEATURE [Part::Cut] Cut229
  Base = -> Fusion184
  Tool = -> Cylinder153
FEATURE [Part::Cut] Cut230
  Base = -> Cut229
  Placement = pos=(-4,10,0) rot=(0,0,1;0rad)
  Tool = -> Cylinder154
FEATURE [Part::MultiFuse] Fusion187
  Shapes = -> [Box315,Box229]
FEATURE [Part::Cut] Cut235
  Base = -> Fusion187
  Tool = -> Cylinder148
FEATURE [Part::Cut] Cut236
  Base = -> Cut235
  Placement = pos=(-4,-10,0) rot=(0,0,1;0rad)
  Tool = -> Cylinder147
FEATURE [Part::MultiFuse] Fusion188
  Shapes = -> [Box349,Box346]
FEATURE [Part::Cut] Cut237
  Base = -> Fusion188
  Tool = -> Cylinder161
FEATURE [Part::Cut] Cut238
  Base = -> Cut237
  Placement = pos=(4,10,0) rot=(0,0,1;0rad)
  Tool = -> Cylinder162
FEATURE [Part::MultiFuse] Fusion191
  Shapes = -> [Box348,Box345]
FEATURE [Part::Cut] Cut243
  Base = -> Fusion191
  Tool = -> Cylinder156
FEATURE [Part::Cut] Cut244
  Base = -> Cut243
  Placement = pos=(4,-10,0) rot=(0,0,1;0rad)
  Tool = -> Cylinder155
FEATURE [Part::Cut] Cut245
  Base = -> Box312
  Placement = pos=(4,-10,0) rot=(0,0,1;0rad)
  Tool = -> Cylinder139
FEATURE [Part::Cut] Cut246
  Base = -> Box302
  Placement = pos=(4,10,0) rot=(0,0,1;0rad)
  Tool = -> Cylinder146
FEATURE [Part::Cut] Cut247
  Base = -> Box307
  Placement = pos=(-4,10,0) rot=(0,0,1;0rad)
  Tool = -> Cylinder140
FEATURE [Part::Box] Box358  label="立方体330"
  AttacherType = Attacher::AttachEngine3D
  Height = 27
  Length = 3
  Placement = pos=(-4.9,-14.9,0) rot=(0,0,1;0rad)
  Width = 10
FEATURE [Part::Cylinder] Cylinder267  label="円柱267"
  Angle = 360
  AttacherType = Attacher::AttachEngine3D
  FirstAngle = 0
  Height = 26
  Placement = pos=(3,0,0) rot=(0,0,1;0rad)
  Radius = 32.5
  SecondAngle = 0
FEATURE [Part::Cylinder] Cylinder268  label="円柱268"
  Angle = 360
  AttacherType = Attacher::AttachEngine3D
  FirstAngle = 0
  Height = 26
  Radius = 2
  SecondAngle = 0
FEATURE [Part::Cut] Cut248  label="タイヤ"
  Base = -> Cylinder267
  Placement = pos=(47,54,10) rot=(0,1,0;1.5708rad)
  Tool = -> Cylinder268
  expr: .Placement.Base.x = 47 mm
FEATURE [Part::Cylinder] Cylinder269  label="円柱269"
  Angle = 360
  AttacherType = Attacher::AttachEngine3D
  FirstAngle = 0
  Height = 26
  Placement = pos=(3,0,0) rot=(0,0,1;0rad)
  Radius = 32.5
  SecondAngle = 0
FEATURE [Part::Cylinder] Cylinder270  label="円柱270"
  Angle = 360
  AttacherType = Attacher::AttachEngine3D
  FirstAngle = 0
  Height = 26
  Radius = 2
  SecondAngle = 0
FEATURE [Part::Cut] Cut249  label="タイヤ001"
  Base = -> Cylinder269
  Placement = pos=(47,-74,10) rot=(0,1,0;1.5708rad)
  Tool = -> Cylinder270
  expr: .Placement.Base.x = 47 mm
FEATURE [Part::Box] Box211  label="二段目　"
  AttacherType = Attacher::AttachEngine3D
  Height = 5
  Length = 144.2
  Placement = pos=(-106,-108,32) rot=(0,0,1;0rad)
  Width = 184
FEATURE [Part::Box] Box  label="リポバッテリー"
  AttacherType = Attacher::AttachEngine3D
  Height = 17
  Length = 36
  Placement = pos=(-11,-17,37) rot=(0,0,1;0rad)
  Width = 80
FEATURE [Part::Box] Box359  label="リボバッテリーケース"
  AttacherType = Attacher::AttachEngine3D
  Height = 20
  Length = 42
  Placement = pos=(-14,-20,37) rot=(0,0,1;0rad)
  Width = 83
FEATURE [Part::Box] Box360  label="立方体331"
  AttacherType = Attacher::AttachEngine3D
  Height = 27
  Length = 3
  Placement = pos=(-65.9,-14.9,0) rot=(0,0,1;0rad)
  Width = 10
FEATURE [Part::Box] Box361  label="立方体332"
  AttacherType = Attacher::AttachEngine3D
  Height = 2
  Length = 64
  Placement = pos=(-65.9,-14.9,27) rot=(0,0,1;0rad)
  Width = 10
FEATURE [Part::Box] Box362  label="立方体333"
  AttacherType = Attacher::AttachEngine3D
  Height = 20.1
  Length = 8.8
  Placement = pos=(25.4,-16.9,0) rot=(0,0,1;0rad)
  Width = 13.9
FEATURE [Part::Box] Box363  label="立方体334"
  AttacherType = Attacher::AttachEngine3D
  Height = 20.1
  Length = 12
  Placement = pos=(-90.5,-16.9,0) rot=(0,0,1;0rad)
  Width = 13.9
FEATURE [Part::Box] Box364  label="立方体335"
  AttacherType = Attacher::AttachEngine3D
  Height = 20.1
  Length = 8.8
  Placement = pos=(-102,-16.9,0) rot=(0,0,1;0rad)
  Width = 13.9
FEATURE [Part::Cut] Cut250  label="リボケース"
  Base = -> Box359
  Placement = pos=(-28,-4,0) rot=(0,0,1;0rad)
  Tool = -> Box
FEATURE [Part::MultiFuse] Fusion192
  Placement = pos=(-16,0,0) rot=(0,0,1;0rad)
  Shapes = -> [Box294,Box296,Box324]
FEATURE [Part::MultiFuse] Fusion193
  Shapes = -> [Cylinder064,Cylinder065,Cylinder066,Cylinder067]
FEATURE [Part::Cut] Cut251
  Base = -> Box260
  Placement = pos=(-4,0,12) rot=(0,0,1;0rad)
  Tool = -> Fusion193
FEATURE [Part::Box] Box295  label="立方体267"
  AttacherType = Attacher::AttachEngine3D
  Height = 3
  Length = 81
  Placement = pos=(-133,66,49) rot=(0,0,1;0rad)
  Width = 10
FEATURE [Part::Box] Box293  label="立方体265"
  AttacherType = Attacher::AttachEngine3D
  Height = 3
  Length = 54
  Placement = pos=(-106,-32,49) rot=(0,0,1;0rad)
  Width = 10
FEATURE [Part::Box] Box365  label="立方体336"
  AttacherType = Attacher::AttachEngine3D
  Height = 13
  Length = 3
  Placement = pos=(-133,66,49) rot=(0,0,1;0rad)
  Width = 10
FEATURE [Part::Box] Box366  label="立方体337"
  AttacherType = Attacher::AttachEngine3D
  Height = 3
  Length = 25
  Placement = pos=(-133,41,49) rot=(0,0,1;0rad)
  Width = 25
FEATURE [Part::Chamfer] Chamfer024
  Base = -> Box366
  EdgeLinks = -> Box366 [Edge1]
  Edges = 1 edges r=24.99: [Edge1]
FEATURE [Part::MultiFuse] Fusion194
  Shapes = -> [Cut251,Box295,Chamfer024,Box293]
FEATURE [Part::MultiFuse] Fusion195
  Shapes = -> [Fusion194,Box365]
FEATURE [Part::MultiFuse] Fusion196
  Shapes = -> [Cylinder198,Cylinder197,Cylinder199,Cylinder196]
FEATURE [Part::Cut] Cut252
  Base = -> Fusion195
  Tool = -> Fusion196
FEATURE [Part::MultiFuse] Fusion197  label=" Coral"
  Shapes = -> [Box297,Box325]
FEATURE [Part::Cylinder] Cylinder271  label="円柱271"
  Angle = 360
  AttacherType = Attacher::AttachEngine3D
  FirstAngle = 0
  Height = 5
  Placement = pos=(-101,-27,32) rot=(0,0,1;0rad)
  Radius = 4
  SecondAngle = 0
FEATURE [Part::Cylinder] Cylinder272  label="円柱272"
  Angle = 360
  AttacherType = Attacher::AttachEngine3D
  FirstAngle = 0
  Height = 5
  Placement = pos=(-57,-27,32) rot=(0,0,1;0rad)
  Radius = 4
  SecondAngle = 0
FEATURE [Part::Cylinder] Cylinder273  label="円柱273"
  Angle = 360
  AttacherType = Attacher::AttachEngine3D
  FirstAngle = 0
  Height = 5
  Placement = pos=(-57,71,32) rot=(0,0,1;0rad)
  Radius = 4
  SecondAngle = 0
FEATURE [Part::Cylinder] Cylinder274  label="円柱274"
  Angle = 360
  AttacherType = Attacher::AttachEngine3D
  FirstAngle = 0
  Height = 5
  Placement = pos=(-101,71,32) rot=(0,0,1;0rad)
  Radius = 4
  SecondAngle = 0
FEATURE [Part::MultiFuse] Fusion198
  Shapes = -> [Cylinder271,Cylinder272,Cylinder273,Cylinder274]
FEATURE [Part::MultiFuse] Fusion199
  Shapes = -> [Cylinder200,Cylinder195,Cylinder201,Cylinder202]
FEATURE [Part::MultiFuse] Fusion200
  Shapes = -> [Box300,Box299,Box298,Box301]
FEATURE [Part::Cylinder] Cylinder275  label="円柱275"
  Angle = 360
  AttacherType = Attacher::AttachEngine3D
  FirstAngle = 0
  Height = 5
  Placement = pos=(-47,-27,32) rot=(0,0,1;0rad)
  Radius = 4
  SecondAngle = 0
FEATURE [Part::Cylinder] Cylinder276  label="円柱276"
  Angle = 360
  AttacherType = Attacher::AttachEngine3D
  FirstAngle = 0
  Height = 5
  Placement = pos=(33,-27,32) rot=(0,0,1;0rad)
  Radius = 4
  SecondAngle = 0
FEATURE [Part::Cylinder] Cylinder277  label="円柱277"
  Angle = 360
  AttacherType = Attacher::AttachEngine3D
  FirstAngle = 0
  Height = 5
  Placement = pos=(-47,63,32) rot=(0,0,1;0rad)
  Radius = 4
  SecondAngle = 0
FEATURE [Part::Cylinder] Cylinder278  label="円柱278"
  Angle = 360
  AttacherType = Attacher::AttachEngine3D
  FirstAngle = 0
  Height = 5
  Placement = pos=(33,63,32) rot=(0,0,1;0rad)
  Radius = 4
  SecondAngle = 0
FEATURE [Part::MultiFuse] Fusion204
  Shapes = -> [Box328,Box327,Box329,Box330]
FEATURE [Part::MultiFuse] Fusion207
  Shapes = -> [Cylinder210,Cylinder207,Cylinder208,Cylinder209]
FEATURE [Part::MultiFuse] Fusion208
  Placement = pos=(0,8,0) rot=(0,0,1;0rad)
  Shapes = -> [Cylinder275,Cylinder276,Cylinder277,Cylinder278]
FEATURE [Part::MultiFuse] Fusion209
  Placement = pos=(0,5,42) rot=(0,0,1;0rad)
  Shapes = -> [Cylinder192,Cylinder191]
FEATURE [Part::Cut] Cut257
  Base = -> Box211
  Tool = -> Box215
FEATURE [Part::MultiFuse] Fusion211
  Placement = pos=(-8.5,-35,138) rot=(1,0,0;1.5708rad)
  Shapes = -> [Box100,Box101]
FEATURE [Part::Box] Box377  label="立方体"
  AttacherType = Attacher::AttachEngine3D
  Height = 8
  Length = 74
  Placement = pos=(-71,-79,37) rot=(0,0,1;0rad)
  Width = 35
FEATURE [Part::Box] Box378  label="立方体348"
  AttacherType = Attacher::AttachEngine3D
  Height = 8
  Length = 36
  Placement = pos=(-52,-55,32) rot=(0,0,1;0rad)
  Width = 31
FEATURE [Part::Cut] Cut259
  Base = -> Box377
  Tool = -> Fusion211
FEATURE [Part::Cut] Cut260
  Base = -> Cut259
  Placement = pos=(0,3,0) rot=(0,0,1;0rad)
  Tool = -> Fusion209
FEATURE [Part::Chamfer] Chamfer025
  Base = -> Cut260
  EdgeLinks = -> Cut260 [Edge2,Edge9]
  Edges = 2 edges r=7.99: [Edge2,Edge9]
FEATURE [Part::Cylinder] Cylinder279  label="円柱279"
  Angle = 360
  AttacherType = Attacher::AttachEngine3D
  FirstAngle = 0
  Height = 5
  Placement = pos=(30.2,-10,15.1) rot=(0,0,1;0rad)
  Radius = 4
  SecondAngle = 0
FEATURE [Part::Cylinder] Cylinder280  label="円柱280"
  Angle = 360
  AttacherType = Attacher::AttachEngine3D
  FirstAngle = 0
  Height = 25.1
  Placement = pos=(17.2,-10,-5) rot=(0,0,1;0rad)
  Radius = 2
  SecondAngle = 0
FEATURE [Part::Cylinder] Cylinder283  label="円柱283"
  Angle = 360
  AttacherType = Attacher::AttachEngine3D
  FirstAngle = 0
  Height = 5
  Placement = pos=(17.2,-10,-5) rot=(0,0,1;0rad)
  Radius = 4
  SecondAngle = 0
FEATURE [Part::Cylinder] Cylinder285  label="円柱285"
  Angle = 360
  AttacherType = Attacher::AttachEngine3D
  FirstAngle = 0
  Height = 10
  Placement = pos=(30.2,-10,15.1) rot=(0,0,1;0rad)
  Radius = 4
  SecondAngle = 0
FEATURE [Part::Cut] Cut261
  Base = -> Box351
  Tool = -> Cylinder280
FEATURE [Part::Cut] Cut262
  Base = -> Box362
  Tool = -> Cylinder279
FEATURE [Part::Box] Box379  label="立方体349"
  AttacherType = Attacher::AttachEngine3D
  Height = 6.9
  Length = 16
  Placement = pos=(22.2,-14,25.1) rot=(0,0,1;0rad)
  Width = 8
FEATURE [Part::Cylinder] Cylinder286  label="円柱286"
  Angle = 360
  AttacherType = Attacher::AttachEngine3D
  FirstAngle = 0
  Height = 10
  Placement = pos=(-98,-10,15.1) rot=(0,0,1;0rad)
  Radius = 4
  SecondAngle = 0
FEATURE [Part::Cylinder] Cylinder287  label="円柱287"
  Angle = 360
  AttacherType = Attacher::AttachEngine3D
  FirstAngle = 0
  Height = 10
  Placement = pos=(-98,-10,15.1) rot=(0,0,1;0rad)
  Radius = 4
  SecondAngle = 0
FEATURE [Part::Cut] Cut263
  Base = -> Box364
  Tool = -> Cylinder287
FEATURE [Part::Cylinder] Cylinder288  label="円柱288"
  Angle = 360
  AttacherType = Attacher::AttachEngine3D
  FirstAngle = 0
  Height = 30.1
  Placement = pos=(-85,-10,-5) rot=(0,0,1;0rad)
  Radius = 2
  SecondAngle = 0
FEATURE [Part::Cylinder] Cylinder289  label="円柱289"
  Angle = 360
  AttacherType = Attacher::AttachEngine3D
  FirstAngle = 0
  Height = 5
  Placement = pos=(-85,-10,-5) rot=(0,0,1;0rad)
  Radius = 4
  SecondAngle = 0
FEATURE [Part::Cut] Cut264
  Base = -> Box363
  Tool = -> Cylinder288
FEATURE [Part::MultiFuse] Fusion216
  Shapes = -> [Cylinder289,Cylinder283]
FEATURE [Part::Box] Box380  label="立方体350"
  AttacherType = Attacher::AttachEngine3D
  Height = 6.9
  Length = 16
  Placement = pos=(-106,-14,25.1) rot=(0,0,1;0rad)
  Width = 8
FEATURE [Part::MultiFuse] Fusion217
  Shapes = -> [Cylinder285,Box379]
FEATURE [Part::MultiFuse] Fusion218
  Shapes = -> [Cylinder286,Box380]
FEATURE [Part::MultiFuse] Fusion219
  Shapes = -> [Fusion217,Fusion218]
FEATURE [Part::Box] Box381  label="立方体351"
  AttacherType = Attacher::AttachEngine3D
  Height = 25
  Length = 15
  Placement = pos=(-41.9,-108,30) rot=(0,0,1;0rad)
  Width = 15
FEATURE [Part::Box] Box382  label="立方体352"
  AttacherType = Attacher::AttachEngine3D
  Height = 25
  Length = 25
  Placement = pos=(-46.9,-94,30) rot=(0,0,1;0rad)
  Width = 1
FEATURE [Part::Box] Box383  label="立方体353"
  AttacherType = Attacher::AttachEngine3D
  Height = 7
  Length = 84
  Placement = pos=(-75.9,-86,32) rot=(0,0,1;0rad)
  Width = 10
FEATURE [Part::MultiFuse] Fusion221
  Placement = pos=(0,-5,-8) rot=(0,0,1;0rad)
  Shapes = -> [Box381,Box382]
FEATURE [Part::MultiFuse] Fusion223
  Shapes = -> [Box024,Box026]
FEATURE [Part::Cut] Cut268
  Base = -> Fusion223
  Placement = pos=(-9,0,10) rot=(0,0,1;0rad)
  Tool = -> Box025
FEATURE [Part::Box] Box384  label="立方体354"
  AttacherType = Attacher::AttachEngine3D
  Height = 2
  Length = 2
  Placement = pos=(-47,-93,26) rot=(0,0,1;0rad)
  Width = 5
FEATURE [Part::Box] Box385  label="立方体355"
  AttacherType = Attacher::AttachEngine3D
  Height = 2
  Length = 2
  Placement = pos=(-24,-93,26) rot=(0,0,1;0rad)
  Width = 5
FEATURE [Part::MultiFuse] Fusion224
  Placement = pos=(0,-5,-4) rot=(0,0,1;0rad)
  Shapes = -> [Box384,Box385,Cut268]
FEATURE [Part::Box] Box386  label="立方体356"
  AttacherType = Attacher::AttachEngine3D
  Height = 31
  Length = 54
  Placement = pos=(-60.9,-108,19) rot=(0,0,1;0rad)
  Width = 12
FEATURE [Part::Box] Box387  label="立方体357"
  AttacherType = Attacher::AttachEngine3D
  Height = 3
  Length = 54
  Placement = pos=(-60.9,-98,47) rot=(0,0,1;0rad)
  Width = 5
FEATURE [Part::Cut] Cut269
  Base = -> Box386
  Tool = -> Box343
FEATURE [Part::Cut] Cut270
  Base = -> Cut269
  Tool = -> Fusion221
FEATURE [Part::Box] Box388  label="立方体358"
  AttacherType = Attacher::AttachEngine3D
  Height = 32
  Length = 6
  Placement = pos=(-66.9,-96,0) rot=(0,0,1;0rad)
  Width = 16
FEATURE [Part::Box] Box390  label="立方体360"
  AttacherType = Attacher::AttachEngine3D
  Height = 32
  Length = 6
  Placement = pos=(-6.9,-96,0) rot=(0,0,1;0rad)
  Width = 16
FEATURE [Part::Box] Box391  label="立方体361"
  AttacherType = Attacher::AttachEngine3D
  Height = 32
  Length = 60
  Placement = pos=(-63.9,-93,0) rot=(0,0,1;0rad)
  Width = 13
FEATURE [Part::Box] Box392  label="立方体362"
  AttacherType = Attacher::AttachEngine3D
  Height = 14
  Length = 84
  Placement = pos=(-75.9,-87,32) rot=(-1,0,0;1.22173rad)
  Width = 10
FEATURE [Part::Cut] Cut273
  Base = -> Box383
  Tool = -> Box392
FEATURE [Part::Fillet] Fillet007
  Base = -> Cut273
  EdgeLinks = -> Cut273 [Edge5]
  Edges = 1 edges r=1: [Edge5]
FEATURE [Part::Box] Box395  label="立方体365"
  AttacherType = Attacher::AttachEngine3D
  Height = 10
  Length = 120
  Placement = pos=(-93.9,-86,27) rot=(0,0,1;0rad)
  Width = 10
FEATURE [Part::Box] Box397  label="立方体367"
  AttacherType = Attacher::AttachEngine3D
  Height = 20
  Length = 33
  Placement = pos=(-42,59,37) rot=(0,0,1;0rad)
  Width = 4
FEATURE [Part::Box] Box398  label="立方体368"
  AttacherType = Attacher::AttachEngine3D
  Height = 3
  Length = 6
  Placement = pos=(-9,59,54) rot=(0,0,1;0rad)
  Width = 4
FEATURE [Part::Box] Box399  label="立方体369"
  AttacherType = Attacher::AttachEngine3D
  Height = 20
  Length = 3
  Placement = pos=(-3,59,37) rot=(0,0,1;0rad)
  Width = 4
FEATURE [Part::MultiFuse] Fusion228
  Shapes = -> [Box398,Box399,Cut250]
FEATURE [Part::Box] Box400  label="立方体370"
  AttacherType = Attacher::AttachEngine3D
  Height = 5
  Length = 33
  Placement = pos=(-42,59,37) rot=(0,0,1;0rad)
  Width = 22
FEATURE [Part::Cylinder] Cylinder290  label="円柱290"
  Angle = 360
  AttacherType = Attacher::AttachEngine3D
  FirstAngle = 0
  Height = 10
  Placement = pos=(-36,72,32) rot=(0,0,1;0rad)
  Radius = 2
  SecondAngle = 0
FEATURE [Part::Cylinder] Cylinder291  label="円柱291"
  Angle = 360
  AttacherType = Attacher::AttachEngine3D
  FirstAngle = 0
  Height = 10
  Placement = pos=(-15,72,32) rot=(0,0,1;0rad)
  Radius = 2
  SecondAngle = 0
FEATURE [Part::MultiFuse] Fusion229
  Shapes = -> [Cylinder290,Cylinder291]
FEATURE [Part::Cylinder] Cylinder292  label="円柱292"
  Angle = 360
  AttacherType = Attacher::AttachEngine3D
  FirstAngle = 0
  Height = 10
  Placement = pos=(-36,72,32) rot=(0,0,1;0rad)
  Radius = 2
  SecondAngle = 0
FEATURE [Part::Cylinder] Cylinder293  label="円柱293"
  Angle = 360
  AttacherType = Attacher::AttachEngine3D
  FirstAngle = 0
  Height = 10
  Placement = pos=(-15,72,32) rot=(0,0,1;0rad)
  Radius = 2
  SecondAngle = 0
FEATURE [Part::MultiFuse] Fusion230
  Shapes = -> [Cylinder292,Cylinder293]
FEATURE [Part::Cut] Cut277
  Base = -> Box400
  Tool = -> Fusion229
FEATURE [Part::MultiFuse] Fusion231  label="リポバッテリー蓋"
  Shapes = -> [Box397,Cut277]
FEATURE [Part::Cut] Cut279
  Base = -> Cut270
  Tool = -> Box387
FEATURE [Part::MultiFuse] Fusion232
  Shapes = -> [Cylinder189,Cylinder190]
FEATURE [Part::Cylinder] Cylinder294  label="円柱294"
  Angle = 360
  AttacherType = Attacher::AttachEngine3D
  FirstAngle = 0
  Height = 20
  Placement = pos=(-53,-88,43) rot=(1,0,0;1.5708rad)
  Radius = 2
  SecondAngle = 0
FEATURE [Part::Cylinder] Cylinder295  label="円柱295"
  Angle = 360
  AttacherType = Attacher::AttachEngine3D
  FirstAngle = 0
  Height = 20
  Placement = pos=(-16,-88,43) rot=(1,0,0;1.5708rad)
  Radius = 2
  SecondAngle = 0
FEATURE [Part::MultiFuse] Fusion233
  Shapes = -> [Cylinder294,Cylinder295]
FEATURE [Part::Cut] Cut280  label="レスキューカメラ蓋"
  Base = -> Fusion224
  Tool = -> Fusion233
FEATURE [Part::Cut] Cut281
  Base = -> Cut279
  Tool = -> Fusion232
FEATURE [Part::MultiFuse] Fusion234
  Shapes = -> [Box360,Box361,Box358]
FEATURE [Part::MultiFuse] Fusion235
  Shapes = -> [Box213,Box214]
FEATURE [Part::Box] Box401  label="立方体371"
  AttacherType = Attacher::AttachEngine3D
  Height = 12
  Length = 3
  Placement = pos=(-65.9,-16.9,0) rot=(0,0,1;0rad)
  Width = 10
FEATURE [Part::Box] Box402  label="立方体372"
  AttacherType = Attacher::AttachEngine3D
  Height = 12
  Length = 3
  Placement = pos=(-4.9,-16.9,0) rot=(0,0,1;0rad)
  Width = 10
FEATURE [Part::MultiFuse] Fusion236
  Placement = pos=(0,54,0) rot=(0,0,1;0rad)
  Shapes = -> [Box401,Box402]
FEATURE [Part::MultiFuse] Fusion237
  Shapes = -> [Box235,Fusion234,Fusion235,Fusion236]
FEATURE [Part::MultiFuse] Fusion238
  Shapes = -> [Cut264,Cut261]
FEATURE [Part::MultiFuse] Fusion239
  Shapes = -> [Cut262,Cut263]
FEATURE [Part::MultiFuse] Fusion240
  Shapes = -> [Fusion238,Fusion239]
FEATURE [Part::MultiFuse] Fusion241
  Shapes = -> [Cut246,Cut247,Cut093,Cut245]
FEATURE [Part::MultiFuse] Fusion242
  Shapes = -> [Cut238,Cut244,Cut230,Cut236]
FEATURE [Part::MultiFuse] Fusion243
  Shapes = -> [Fusion240,Fusion241,Fusion242]
FEATURE [Part::Box] Box403  label="立方体373"
  AttacherType = Attacher::AttachEngine3D
  Height = 25
  Length = 30
  Placement = pos=(-48.9,-108,22) rot=(0,0,1;0rad)
  Width = 5
FEATURE [Part::Cut] Cut282
  Base = -> Cut281
  Tool = -> Box403
FEATURE [Part::Box] Box404  label="立方体374"
  AttacherType = Attacher::AttachEngine3D
  Height = 15
  Length = 10
  Placement = pos=(-70.9,-108,22) rot=(0,0,1;0rad)
  Width = 9
FEATURE [Part::Box] Box405  label="立方体375"
  AttacherType = Attacher::AttachEngine3D
  Height = 15
  Length = 10
  Placement = pos=(-6.9,-108,22) rot=(0,0,1;0rad)
  Width = 9
FEATURE [Part::Chamfer] Chamfer029
  Base = -> Box404
  EdgeLinks = -> Box404 [Edge4]
  Edges = 1 edges r=9.99: [Edge4]
FEATURE [Part::Chamfer] Chamfer030
  Base = -> Box405
  EdgeLinks = -> Box405 [Edge8]
  Edges = 1 edges r=9.99: [Edge8]
FEATURE [Part::MultiFuse] Fusion244
  Shapes = -> [Cut282,Chamfer029,Chamfer030]
FEATURE [Part::Box] Box406  label="立方体376"
  AttacherType = Attacher::AttachEngine3D
  Height = 5
  Length = 16
  Placement = pos=(-82.9,-108,37) rot=(0,0,1;0rad)
  Width = 20
FEATURE [Part::Box] Box407  label="立方体377"
  AttacherType = Attacher::AttachEngine3D
  Height = 5
  Length = 16
  Placement = pos=(-0.9,-108,37) rot=(0,0,1;0rad)
  Width = 20
FEATURE [Part::MultiFuse] Fusion246
  Placement = pos=(0,2,4) rot=(0,0,1;0rad)
  Shapes = -> [Cylinder181,Cylinder182]
FEATURE [Part::MultiFuse] Fusion247
  Placement = pos=(0,2,4) rot=(0,0,1;0rad)
  Shapes = -> [Cylinder179,Cylinder180]
FEATURE [Part::Box] Box408  label="立方体378"
  AttacherType = Attacher::AttachEngine3D
  Height = 20.1
  Length = 27.3
  Placement = pos=(-71.6,-58.9,62) rot=(0,0,1;0rad)
  Width = 9
FEATURE [Part::Box] Box409  label="立方体379"
  AttacherType = Attacher::AttachEngine3D
  Height = 25
  Length = 6
  Placement = pos=(-66.9,-64.9,37) rot=(0,0,1;0rad)
  Width = 15
FEATURE [Part::Box] Box410  label="立方体380"
  AttacherType = Attacher::AttachEngine3D
  Height = 5
  Length = 16
  Placement = pos=(-82.9,-64.9,37) rot=(0,0,1;0rad)
  Width = 15
FEATURE [Part::Box] Box411  label="立方体381"
  AttacherType = Attacher::AttachEngine3D
  Height = 25
  Length = 6
  Placement = pos=(-6.9,-64.9,37) rot=(0,0,1;0rad)
  Width = 15
FEATURE [Part::Box] Box412  label="立方体382"
  AttacherType = Attacher::AttachEngine3D
  Height = 5
  Length = 16
  Placement = pos=(-0.9,-64.9,37) rot=(0,0,1;0rad)
  Width = 15
FEATURE [Part::MultiFuse] Fusion249
  Shapes = -> [Box406,Box286,Box407,Box288]
FEATURE [Part::MultiFuse] Fusion251
  Shapes = -> [Box283,Box281,Box408]
FEATURE [Part::MultiFuse] Fusion252
  Shapes = -> [Fusion246,Fusion247]
FEATURE [Part::Cut] Cut283
  Base = -> Fusion251
  Tool = -> Fusion252
FEATURE [Part::Box] Box413  label="立方体383"
  AttacherType = Attacher::AttachEngine3D
  Height = 5
  Length = 8.9
  Placement = pos=(-60.9,-45,32) rot=(0,0,1;0rad)
  Width = 8
FEATURE [Part::Box] Box414  label="立方体384"
  AttacherType = Attacher::AttachEngine3D
  Height = 5
  Length = 9.1
  Placement = pos=(-16,-45,32) rot=(0,0,1;0rad)
  Width = 8
FEATURE [Part::Box] Box415  label="立方体385"
  AttacherType = Attacher::AttachEngine3D
  Height = 3
  Length = 36
  Placement = pos=(-52,-45,54) rot=(0,0,1;0rad)
  Width = 21
FEATURE [Part::Box] Box416  label="立方体386"
  AttacherType = Attacher::AttachEngine3D
  Height = 25
  Length = 3
  Placement = pos=(-52,-45,32) rot=(0,0,1;0rad)
  Width = 21
FEATURE [Part::Box] Box417  label="立方体387"
  AttacherType = Attacher::AttachEngine3D
  Height = 25
  Length = 3
  Placement = pos=(-19,-45,32) rot=(0,0,1;0rad)
  Width = 21
FEATURE [Part::MultiFuse] Fusion257
  Shapes = -> [Box413,Box414,Box415,Box416,Box417]
FEATURE [Part::FeaturePython] Tube008  # WARN: FeaturePython — macro-defined, semantics opaque (R4)
  AttacherType = Attacher::AttachEngine3D
  Height = 40
  InnerRadius = 30
  OuterRadius = 33
  Placement = pos=(-34,-160,5) rot=(0,0,1;0rad)
FEATURE [Part::Cut] Cut052
  Base = -> Sphere
  Tool = -> Sphere001
FEATURE [Part::Box] Box418  label="立方体388"
  AttacherType = Attacher::AttachEngine3D
  Height = 67
  Length = 15
  Placement = pos=(-31.3,-161,15) rot=(0,0,1;0rad)
  Width = 49
FEATURE [Part::Cylinder] Cylinder302  label="円柱302"
  Angle = 360
  AttacherType = Attacher::AttachEngine3D
  FirstAngle = 0
  Height = 50
  Placement = pos=(-31.3,-131,58) rot=(0.57735,0.57735,0.57735;2.0944rad)
  Radius = 12
  SecondAngle = 0
FEATURE [Part::FeaturePython] CycloidGear016  # WARN: FeaturePython — macro-defined, semantics opaque (R4)
  AttacherType = Attacher::AttachEngine3D
  Placement = pos=(-32.8,-89,72) rot=(0,1,0;1.5708rad)
  angular_backlash = 0
  backlash = 0
  clearance = 0.25
  double_helix = false
  head = 0
  head_fillet = 0
  height = 5.5
  helix_angle = 0
  inner_diameter = 12.5
  module = 0.24
  num_teeth = 25
  numpoints = 20
  outer_diameter = 7.5
  pitch_diameter = 6
  root_fillet = 0
  version = 1.3.0
  expr: angular_backlash = backlash / pitch_diameter * 360 ° / pi
  expr: inner_diameter = num_teeth / 2
  expr: pitch_diameter = num_teeth * module
FEATURE [Part::Cylinder] Cylinder303  label="円柱303"
  Angle = 360
  AttacherType = Attacher::AttachEngine3D
  FirstAngle = 0
  Height = 15
  Placement = pos=(-31.3,-89,72) rot=(0.57735,0.57735,0.57735;2.0944rad)
  Radius = 1.5
  SecondAngle = 0
FEATURE [Part::Box] Box419  label="立方体389"
  AttacherType = Attacher::AttachEngine3D
  Height = 3
  Length = 13
  Placement = pos=(-133,66,62) rot=(0,0,1;0rad)
  Width = 10
FEATURE [Part::MultiFuse] Fusion262  label="ラズパイ固定関節材"
  Shapes = -> [Cut252,Box419]
FEATURE [Part::Box] Box422  label="立方体392"
  AttacherType = Attacher::AttachEngine3D
  Height = 4
  Length = 81.6
  Placement = pos=(-75.2,65,0) rot=(0,0,1;0rad)
  Width = 10
FEATURE [Part::Box] Box423  label="立方体393"
  AttacherType = Attacher::AttachEngine3D
  Height = 12
  Length = 25
  Placement = pos=(-75.2,65,0) rot=(0,0,1;0rad)
  Width = 10
FEATURE [Part::Box] Box424  label="立方体394"
  AttacherType = Attacher::AttachEngine3D
  Height = 12
  Length = 25
  Placement = pos=(-18.6,65,0) rot=(0,0,1;0rad)
  Width = 10
FEATURE [Part::Box] Box425  label="立方体395"
  AttacherType = Attacher::AttachEngine3D
  Height = 12
  Length = 10
  Placement = pos=(-60.2,54.6,0) rot=(0,0,1;0rad)
  Width = 20.4
FEATURE [Part::Box] Box426  label="立方体396"
  AttacherType = Attacher::AttachEngine3D
  Height = 12
  Length = 10
  Placement = pos=(-18.6,54.6,0) rot=(0,0,1;0rad)
  Width = 20.4
FEATURE [Part::MultiFuse] Fusion269
  Shapes = -> [Box422,Box423,Box424,Box425,Box426]
FEATURE [Part::Fillet] Fillet010
  Base = -> Fusion269
  EdgeLinks = -> Fusion269 [Edge8,Edge10]
  Edges = 2 edges r=4.99: [Edge8,Edge10]
FEATURE [Part::Fillet] Fillet011
  Base = -> Fillet010
  EdgeLinks = -> Fillet010 [Edge88,Edge90]
  Edges = 2 edges r=4.99: [Edge88,Edge90]
FEATURE [Part::Fillet] Fillet012
  Base = -> Fillet011
  EdgeLinks = -> Fillet011 [Edge38,Edge55,Edge73,Edge90]
  Edges = 4 edges r=3: [Edge38,Edge55,Edge73,Edge90]
FEATURE [Part::Fillet] Fillet013
  Base = -> Fillet012
  EdgeLinks = -> Fillet012 [Edge28,Edge48]
  Edges = 2 edges r=2: [Edge28,Edge48]
FEATURE [Part::MultiFuse] Fusion270
  Shapes = -> [Cylinder265,Cylinder264]
FEATURE [Part::Cylinder] Cylinder304  label="円柱304"
  Angle = 360
  AttacherType = Attacher::AttachEngine3D
  FirstAngle = 0
  Height = 12
  Placement = pos=(1.4,70,0) rot=(0,0,1;0rad)
  Radius = 2
  SecondAngle = 0
FEATURE [Part::Cylinder] Cylinder305  label="円柱305"
  Angle = 360
  AttacherType = Attacher::AttachEngine3D
  FirstAngle = 0
  Height = 12
  Placement = pos=(-70.2,70,0) rot=(0,0,1;0rad)
  Radius = 2
  SecondAngle = 0
FEATURE [Part::MultiFuse] Fusion271
  Shapes = -> [Cylinder305,Cylinder304]
FEATURE [Part::Cut] Cut295  label="バッテリー固定材"
  Base = -> Fillet013
  Tool = -> Fusion270
FEATURE [Part::MultiFuse] Fusion273
  Placement = pos=(0,-5,0) rot=(0,0,1;0rad)
  Shapes = -> [Cylinder227,Cylinder229]
FEATURE [Part::Cylinder] Cylinder308  label="円柱308"
  Angle = 360
  AttacherType = Attacher::AttachEngine3D
  FirstAngle = 0
  Height = 42
  Placement = pos=(-81.9,72,-5) rot=(0,0,1;0rad)
  Radius = 2
  SecondAngle = 0
FEATURE [Part::Cylinder] Cylinder309  label="円柱309"
  Angle = 360
  AttacherType = Attacher::AttachEngine3D
  FirstAngle = 0
  Height = 42
  Placement = pos=(14.1,72,-5) rot=(0,0,1;0rad)
  Radius = 2
  SecondAngle = 0
FEATURE [Part::MultiFuse] Fusion275
  Placement = pos=(0,-5,0) rot=(0,0,1;0rad)
  Shapes = -> [Cylinder308,Cylinder309]
FEATURE [Part::Cylinder] Cylinder311  label="円柱311"
  Angle = 360
  AttacherType = Attacher::AttachEngine3D
  FirstAngle = 0
  Height = 47
  Placement = pos=(-75,-98,-5) rot=(0,0,1;0rad)
  Radius = 2
  SecondAngle = 0
FEATURE [Part::Box] Box427  label="立方体397"
  AttacherType = Attacher::AttachEngine3D
  Height = 13
  Length = 30
  Placement = pos=(-94,-22,34) rot=(0,0,1;0rad)
  Width = 65
FEATURE [Part::Box] Box428  label="立方体398"
  AttacherType = Attacher::AttachEngine3D
  Height = 13
  Length = 12
  Placement = pos=(-85,-32,34) rot=(0,0,1;0rad)
  Width = 10
FEATURE [Part::MultiFuse] Fusion281  label=" Coral001"
  Placement = pos=(-9,0,0) rot=(0,0,1;0rad)
  Shapes = -> [Box427,Box428]
FEATURE [Part::MultiFuse] Fusion283
  Shapes = -> [Cylinder084,Sphere003]
FEATURE [Part::Fillet] Fillet014
  Base = -> Box418
  EdgeLinks = -> Box418 [Edge10]
  Edges = 1 edges r=48.99: [Edge10]
  Placement = pos=(4.7,0,0) rot=(0,0,1;0rad)
FEATURE [Part::Box] Box429  label="立方体399"
  AttacherType = Attacher::AttachEngine3D
  Height = 35
  Length = 12.1
  Placement = pos=(-1,-120,-20) rot=(0,0,1;0rad)
  Width = 14
FEATURE [Part::MultiFuse] Fusion117
  Shapes = -> [Cut052,Tube008,Chamfer016]
FEATURE [Part::Cut] Cut054
  Base = -> Fusion117
  Tool = -> Cylinder073
FEATURE [Part::Cut] Cut055
  Base = -> Cut054
  Placement = pos=(0,15,-20) rot=(0,0,1;0rad)
  Tool = -> Cylinder074
FEATURE [Part::Cut] Cut301
  Base = -> Cut057
  Placement = pos=(0,-6,5) rot=(0,0,1;0rad)
  Tool = -> Box429
FEATURE [Part::MultiFuse] Fusion284
  Placement = pos=(0,0,-2) rot=(0,0,1;0rad)
  Shapes = -> [Cut055,Cut301]
FEATURE [Part::MultiFuse] Fusion288
  Shapes = -> [Cylinder303,CycloidGear016]
FEATURE [Part::Cylinder] Cylinder  label="円柱"
  Angle = 360
  AttacherType = Attacher::AttachEngine3D
  FirstAngle = 0
  Height = 50
  Radius = 1
  SecondAngle = 0
FEATURE [Part::Cylinder] Cylinder318  label="円柱318"
  Angle = 360
  AttacherType = Attacher::AttachEngine3D
  FirstAngle = 0
  Height = 50
  Placement = pos=(0,-27.7,0) rot=(0,0,1;0rad)
  Radius = 1
  SecondAngle = 0
FEATURE [Part::MultiFuse] Fusion290
  Placement = pos=(4.1,-87,13.1) rot=(1,0,0;1.5708rad)
  Shapes = -> [Cylinder,Cylinder318]
FEATURE [Part::MultiFuse] Fusion291
  Shapes = -> [Cylinder083,Box289]
FEATURE [Part::Cut] Cut310
  Base = -> Fusion291
  Placement = pos=(4.7,0,0) rot=(0,0,1;0rad)
  Tool = -> Fusion288
FEATURE [Part::Box] Box430  label="立方体400"
  AttacherType = Attacher::AttachEngine3D
  Height = 20.1
  Length = 6
  Placement = pos=(-66.5,-108,62) rot=(0,0,1;0rad)
  Width = 9
FEATURE [Part::Sphere] Sphere004  label="球体004"
  Angle1 = -90
  Angle2 = 90
  Angle3 = 360
  AttacherType = Attacher::AttachEngine3D
  Placement = pos=(-16,-108,43) rot=(0,0,1;0rad)
  Radius = 10
FEATURE [Part::Box] Box431  label="立方体401"
  AttacherType = Attacher::AttachEngine3D
  Height = 35
  Length = 45.1
  Placement = pos=(-34,-146,-17) rot=(0,0,1;0rad)
  Width = 25
FEATURE [Part::Box] Box432  label="立方体402"
  AttacherType = Attacher::AttachEngine3D
  Height = 32.3
  Length = 12.1
  Placement = pos=(0,8.5,-4.9) rot=(0,0,1;0rad)
  Width = 2.5
FEATURE [Part::Box] Box433  label="立方体403"
  AttacherType = Attacher::AttachEngine3D
  Height = 22.5
  Length = 12.1
  Width = 26.7
FEATURE [Part::Box] Box434  label="立方体404"
  AttacherType = Attacher::AttachEngine3D
  Height = 35
  Length = 12.1
  Placement = pos=(-1,-120,-20) rot=(0,0,1;0rad)
  Width = 14
FEATURE [Part::Cone] Cone002  label="円錐002"
  Angle = 360
  AttacherType = Attacher::AttachEngine3D
  Height = 5
  Radius1 = 38
  Radius2 = 33
FEATURE [Part::Cone] Cone003  label="円錐003"
  Angle = 360
  AttacherType = Attacher::AttachEngine3D
  Height = 5
  Radius1 = 33
  Radius2 = 30
FEATURE [Part::Cut] Cut314
  Base = -> Cone002
  Placement = pos=(-34,-160,0) rot=(0,0,1;0rad)
  Tool = -> Cone003
FEATURE [Part::Chamfer] Chamfer034
  Base = -> Cut314
  EdgeLinks = -> Cut314 [Edge3]
  Edges = 1 edges r=2: [Edge3]
FEATURE [Part::Cylinder] Cylinder319  label="円柱319"
  Angle = 360
  AttacherType = Attacher::AttachEngine3D
  FirstAngle = 0
  Height = 20
  Placement = pos=(-60,-160,-3) rot=(0,-1,0;0.785398rad)
  Radius = 1
  SecondAngle = 0
FEATURE [Part::Cylinder] Cylinder320  label="円柱320"
  Angle = 360
  AttacherType = Attacher::AttachEngine3D
  FirstAngle = 0
  Height = 20
  Placement = pos=(-8,-160,-3) rot=(0,1,0;0.785398rad)
  Radius = 1
  SecondAngle = 0
FEATURE [Part::Cylinder] Cylinder321  label="円柱321"
  Angle = 360
  AttacherType = Attacher::AttachEngine3D
  FirstAngle = 0
  Height = 50
  Placement = pos=(-34,-160,-17) rot=(0,0,1;0rad)
  Radius = 33
  SecondAngle = 0
FEATURE [Part::Cylinder] Cylinder322  label="円柱322"
  Angle = 360
  AttacherType = Attacher::AttachEngine3D
  FirstAngle = 0
  Height = 3
  Placement = pos=(6.05,0,16.4) rot=(1,0,0;1.5708rad)
  Radius = 2.4
  SecondAngle = 0
FEATURE [Part::MultiFuse] Fusion294
  Placement = pos=(-1,-151,-12) rot=(0,0,1;0rad)
  Shapes = -> [Cylinder322,Box432,Box433]
FEATURE [Part::Cut] Cut317
  Base = -> Box431
  Tool = -> Fusion294
FEATURE [Part::Cut] Cut318
  Base = -> Cut317
  Placement = pos=(0,15,-3) rot=(0,0,1;0rad)
  Tool = -> Cylinder321
FEATURE [Part::Cut] Cut319
  Base = -> Cut318
  Placement = pos=(0,-6,5) rot=(0,0,1;0rad)
  Tool = -> Box434
FEATURE [Part::Sphere] Sphere005  label="球体005"
  Angle1 = 0
  Angle2 = 60
  Angle3 = 360
  AttacherType = Attacher::AttachEngine3D
  Placement = pos=(-34,-160,45) rot=(0,0,1;0rad)
  Radius = 33
FEATURE [Part::Sphere] Sphere006  label="球体006"
  Angle1 = 0
  Angle2 = 60
  Angle3 = 360
  AttacherType = Attacher::AttachEngine3D
  Placement = pos=(-34,-160,45) rot=(0,0,1;0rad)
  Radius = 30
FEATURE [Part::Cut] Cut313
  Base = -> Sphere005
  Tool = -> Sphere006
FEATURE [Part::FeaturePython] Tube019  # WARN: FeaturePython — macro-defined, semantics opaque (R4)
  AttacherType = Attacher::AttachEngine3D
  Height = 40
  InnerRadius = 30
  OuterRadius = 33
  Placement = pos=(-34,-160,5) rot=(0,0,1;0rad)
FEATURE [Part::MultiFuse] Fusion293
  Shapes = -> [Cut313,Tube019,Chamfer034]
FEATURE [Part::Cut] Cut315
  Base = -> Fusion293
  Tool = -> Cylinder319
FEATURE [Part::Cut] Cut316
  Base = -> Cut315
  Placement = pos=(0,15,-20) rot=(0,0,1;0rad)
  Tool = -> Cylinder320
FEATURE [Part::MultiFuse] Fusion295
  Placement = pos=(0,0,-2) rot=(0,0,1;0rad)
  Shapes = -> [Cut316,Cut319]
FEATURE [Part::Cut] Cut320
  Base = -> Cylinder302
  Tool = -> Fusion295
FEATURE [Part::MultiFuse] Fusion296
  Shapes = -> [Cut320,Sphere004]
FEATURE [Part::Cut] Cut322
  Base = -> Fusion204
  Placement = pos=(0,8,0) rot=(0,0,1;0rad)
  Refine = true
  Tool = -> Fusion207
FEATURE [Part::Fillet] Fillet
  Base = -> Box102
  EdgeLinks = -> Box102 [Edge1,Edge3,Edge5,Edge7]
  Edges = 4 edges r=2: [Edge1,Edge3,Edge5,Edge7]
FEATURE [Part::Cut] Cut324
  Base = -> Cut257
  Refine = true
  Tool = -> Box378
FEATURE [Part::Cut] Cut328
  Base = -> Fusion200
  Refine = true
  Tool = -> Fusion199
FEATURE [Part::Fuse] Fusion300
  Base = -> Fusion198
  Refine = true
  Tool = -> Fusion208
FEATURE [Part::Fuse] Fusion301
  Base = -> Fusion230
  Refine = true
  Tool = -> Fusion300
FEATURE [Part::MultiFuse] Fusion304
  Refine = true
  Shapes = -> [Fusion219,Cut322]
FEATURE [Part::MultiFuse] Fusion305
  Refine = true
  Shapes = -> [Fusion304,Cut328]
FEATURE [Part::Fillet] Fillet015
  Base = -> Box391
  EdgeLinks = -> Box391 [Edge1,Edge5]
  Edges = 2 edges r=2: [Edge1,Edge5]
FEATURE [Part::MultiFuse] Fusion307
  Refine = true
  Shapes = -> [Box390,Box388]
FEATURE [Part::Cut] Cut331
  Base = -> Fusion307
  Placement = pos=(0,-3,0) rot=(0,0,1;0rad)
  Refine = true
  Tool = -> Fillet015
FEATURE [Part::Cut] Cut332
  Base = -> Box268
  Refine = true
  Tool = -> Fusion113
FEATURE [Part::Chamfer] Chamfer035
  Base = -> Cut332
  EdgeLinks = -> Cut332 [Edge27,Edge28]
  Edges = 2 edges r=1.5: [Edge27,Edge28]
  Placement = pos=(0,10,0) rot=(0,0,1;0rad)
FEATURE [Part::Cut] Cut333
  Base = -> Box266
  Refine = true
  Tool = -> Fusion112
FEATURE [Part::Cut] Cut334
  Base = -> Box016
  Refine = true
  Tool = -> Fillet
FEATURE [Part::Chamfer] Chamfer
  Base = -> Cut331
  EdgeLinks = -> Cut331 [Edge8,Edge29]
  Edges = 2 edges r=10: [Edge8,Edge29]
FEATURE [Part::MultiFuse] Fusion311
  Refine = true
  Shapes = -> [Box254,Cut334]
FEATURE [Part::Cut] Cut335
  Base = -> Fusion311
  Refine = true
  Tool = -> Fusion040
FEATURE [Part::Cut] Cut336
  Base = -> Cut283
  Placement = pos=(4.7,0,0) rot=(0,0,1;0rad)
  Refine = true
  Tool = -> Box430
FEATURE [Part::MultiFuse] Fusion313
  Refine = true
  Shapes = -> [Cylinder212,Cylinder311]
FEATURE [Part::Cylinder] Cylinder323  label="円柱323"
  Angle = 360
  AttacherType = Attacher::AttachEngine3D
  FirstAngle = 0
  Height = 47
  Placement = pos=(7,-98,-5) rot=(0,0,1;0rad)
  Radius = 2
  SecondAngle = 0
FEATURE [Part::Cylinder] Cylinder324  label="円柱324"
  Angle = 360
  AttacherType = Attacher::AttachEngine3D
  FirstAngle = 0
  Height = 47
  Placement = pos=(-75,-98,-5) rot=(0,0,1;0rad)
  Radius = 2
  SecondAngle = 0
FEATURE [Part::MultiFuse] Fusion314
  Placement = pos=(0,41,0) rot=(0,0,1;0rad)
  Refine = true
  Shapes = -> [Cylinder323,Cylinder324]
FEATURE [Part::Cylinder] Cylinder325  label="円柱325"
  Angle = 360
  AttacherType = Attacher::AttachEngine3D
  FirstAngle = 0
  Height = 47
  Placement = pos=(7,-98,-5) rot=(0,0,1;0rad)
  Radius = 2
  SecondAngle = 0
FEATURE [Part::Cylinder] Cylinder326  label="円柱326"
  Angle = 360
  AttacherType = Attacher::AttachEngine3D
  FirstAngle = 0
  Height = 47
  Placement = pos=(-75,-98,-5) rot=(0,0,1;0rad)
  Radius = 2
  SecondAngle = 0
FEATURE [Part::MultiFuse] Fusion315
  Refine = true
  Shapes = -> [Cylinder325,Cylinder326]
FEATURE [Part::Cylinder] Cylinder327  label="円柱327"
  Angle = 360
  AttacherType = Attacher::AttachEngine3D
  FirstAngle = 0
  Height = 47
  Placement = pos=(7,-98,-5) rot=(0,0,1;0rad)
  Radius = 2
  SecondAngle = 0
FEATURE [Part::Cylinder] Cylinder328  label="円柱328"
  Angle = 360
  AttacherType = Attacher::AttachEngine3D
  FirstAngle = 0
  Height = 47
  Placement = pos=(-75,-98,-5) rot=(0,0,1;0rad)
  Radius = 2
  SecondAngle = 0
FEATURE [Part::MultiFuse] Fusion316
  Refine = true
  Shapes = -> [Cylinder327,Cylinder328]
FEATURE [Part::Cylinder] Cylinder329  label="円柱329"
  Angle = 360
  AttacherType = Attacher::AttachEngine3D
  FirstAngle = 0
  Height = 47
  Placement = pos=(7,-98,-5) rot=(0,0,1;0rad)
  Radius = 2
  SecondAngle = 0
FEATURE [Part::Cylinder] Cylinder330  label="円柱330"
  Angle = 360
  AttacherType = Attacher::AttachEngine3D
  FirstAngle = 0
  Height = 47
  Placement = pos=(-75,-98,-5) rot=(0,0,1;0rad)
  Radius = 2
  SecondAngle = 0
FEATURE [Part::MultiFuse] Fusion317
  Placement = pos=(0,41,0) rot=(0,0,1;0rad)
  Refine = true
  Shapes = -> [Cylinder329,Cylinder330]
FEATURE [Part::MultiFuse] Fusion318
  Refine = true
  Shapes = -> [Fusion273,Fusion313]
FEATURE [Part::Cut] Cut177
  Base = -> Cylinder011
  Placement = pos=(-8.2,0,0) rot=(0,0,1;0rad)
  Tool = -> Cylinder213
FEATURE [Part::MultiFuse] Fusion319
  Placement = pos=(0,-5,0) rot=(0,0,1;0rad)
  Refine = true
  Shapes = -> [Cut191,Cut196]
FEATURE [Part::MultiFuse] Fusion320
  Refine = true
  Shapes = -> [Fusion243,Fusion237,Fusion271,Chamfer]
FEATURE [Part::MultiFuse] Fusion322
  Refine = true
  Shapes = -> [Box412,Box411,Box409,Box410]
FEATURE [Part::MultiFuse] Fusion323
  Refine = true
  Shapes = -> [Fusion249]
FEATURE [Part::Cut] Cut337
  Base = -> Fusion323
  Refine = true
  Tool = -> Fusion315
FEATURE [Part::Cut] Cut338
  Base = -> Fusion322
  Refine = true
  Tool = -> Fusion314
FEATURE [Part::MultiFuse] Fusion324
  Refine = true
  Shapes = -> [Cut337,Cut338,Cut336]
FEATURE [Part::MultiFuse] Fusion325
  Refine = true
  Shapes = -> [Cut177,Cut182]
FEATURE [Part::MultiFuse] Fusion326
  Refine = true
  Shapes = -> [Fusion319,Fusion325]
FEATURE [Part::MultiFuse] Fusion327
  Refine = true
  Shapes = -> [Fusion216,Fusion318]
FEATURE [Part::MultiFuse] Fusion328
  Refine = true
  Shapes = -> [Fusion316,Fusion317,Fusion275]
FEATURE [Part::Chamfer] Chamfer036
  Base = -> Cut335
  EdgeLinks = -> Cut335 [Edge1,Edge8]
  Edges = 2 edges r=20: [Edge1,Edge8]
FEATURE [Part::Chamfer] Chamfer037
  Base = -> Chamfer036
  EdgeLinks = -> Chamfer036 [Edge3,Edge25]
  Edges = 2 edges r=15: [Edge3,Edge25]
FEATURE [Part::Chamfer] Chamfer038
  Base = -> Cut333
  EdgeLinks = -> Cut333 [Edge16,Edge18]
  Edges = 2 edges r=1.5: [Edge16,Edge18]
  Placement = pos=(0,10,0) rot=(0,0,1;0rad)
FEATURE [Part::MultiFuse] Fusion333
  Refine = true
  Shapes = -> [Chamfer037,Fusion320]
FEATURE [Part::Cut] Cut340
  Base = -> Fusion333
  Refine = true
  Tool = -> Fusion327
FEATURE [Part::Cut] Cut341
  Base = -> Fillet014
  Refine = true
  Tool = -> Fusion283
FEATURE [Part::Cut] Cut342
  Base = -> Cut341
  Refine = true
  Tool = -> Fusion296
FEATURE [Part::Cut] Cut343
  Base = -> Fusion284
  Refine = true
  Tool = -> Fusion290
FEATURE [Part::MultiFuse] Fusion334
  Refine = true
  Shapes = -> [Cut343,Cut342,Cut310]
FEATURE [Part::Box] Box435  label="立方体405"
  AttacherType = Attacher::AttachEngine3D
  Height = 5
  Length = 22
  Placement = pos=(0,-24,32) rot=(0,0,1;0rad)
  Width = 84
FEATURE [Part::Box] Box436  label="立方体406"
  AttacherType = Attacher::AttachEngine3D
  Height = 5
  Length = 28
  Placement = pos=(-70,-14,32) rot=(0,0,1;0rad)
  Width = 75
FEATURE [Part::Box] Box437  label="立方体407"
  AttacherType = Attacher::AttachEngine3D
  Height = 10
  Length = 12
  Placement = pos=(26.2,-90,37) rot=(0,0,1;0rad)
  Width = 34
FEATURE [Part::Box] Box438  label="立方体408"
  AttacherType = Attacher::AttachEngine3D
  Height = 10
  Length = 12
  Placement = pos=(-106,-90,37) rot=(0,0,1;0rad)
  Width = 34
FEATURE [Part::Cut] Cut344
  Base = -> Chamfer035
  Placement = pos=(0,10,0) rot=(0,0,1;0rad)
  Refine = true
  Tool = -> Box437
FEATURE [Part::Cut] Cut345
  Base = -> Cut324
  Refine = true
  Tool = -> Box395
FEATURE [Part::Cut] Cut346
  Base = -> Chamfer038
  Placement = pos=(0,10,0) rot=(0,0,1;0rad)
  Refine = true
  Tool = -> Box438
FEATURE [Part::MultiFuse] Fusion335
  Refine = true
  Shapes = -> [Cut346,Chamfer025,Fillet007,Fusion244,Cut344]
FEATURE [Part::MultiFuse] Fusion336
  Refine = true
  Shapes = -> [Fusion192,Fusion228,Fusion257]
FEATURE [Part::MultiFuse] Fusion337
  Refine = true
  Shapes = -> [Fusion335,Fusion336,Fusion305]
FEATURE [Part::Cut] Cut347
  Base = -> Cut345
  Refine = true
  Tool = -> Fusion281
FEATURE [Part::Chamfer] Chamfer039
  Base = -> Cut347
  EdgeLinks = -> Cut347 [Edge1,Edge54]
  Edges = 2 edges r=20: [Edge1,Edge54]
FEATURE [Part::Box] Box439  label="立方体409"
  AttacherType = Attacher::AttachEngine3D
  Height = 25
  Length = 6
  Placement = pos=(-66.9,-64.9,37) rot=(0,0,1;0rad)
  Width = 15
FEATURE [Part::Box] Box440  label="立方体410"
  AttacherType = Attacher::AttachEngine3D
  Height = 5
  Length = 16
  Placement = pos=(-82.9,-64.9,37) rot=(0,0,1;0rad)
  Width = 15
FEATURE [Part::Box] Box441  label="立方体411"
  AttacherType = Attacher::AttachEngine3D
  Height = 25
  Length = 6
  Placement = pos=(-6.9,-64.9,37) rot=(0,0,1;0rad)
  Width = 15
FEATURE [Part::Box] Box442  label="立方体412"
  AttacherType = Attacher::AttachEngine3D
  Height = 5
  Length = 16
  Placement = pos=(-0.9,-64.9,37) rot=(0,0,1;0rad)
  Width = 15
FEATURE [Part::MultiFuse] Fusion338
  Refine = true
  Shapes = -> [Box442,Box441,Box439,Box440]
FEATURE [Part::Cut] Cut348
  Base = -> Fusion337
  Refine = true
  Tool = -> Fusion338
FEATURE [Part::Cut] Cut349
  Base = -> Chamfer039
  Refine = true
  Tool = -> Fusion328
FEATURE [Part::MultiFuse] Fusion339
  Refine = true
  Shapes = -> [Cut348,Cut349]
FEATURE [Part::MultiFuse] Fusion340
  Refine = true
  Shapes = -> [Box435,Box436]
FEATURE [Part::Cut] Cut350
  Base = -> Fusion339
  Refine = true
  Tool = -> Fusion301
FEATURE [Part::Cut] Cut351
  Base = -> Cut350
  Refine = true
  Tool = -> Fusion340
FEATURE [Part::Box] Box443  label="立方体413"
  AttacherType = Attacher::AttachEngine3D
  Height = 12
  Length = 2
  Placement = pos=(-70.2,65,0) rot=(0,0,1;0rad)
  Width = 10
FEATURE [Part::Cylinder] Cylinder331  label="円柱331"
  Angle = 180
  AttacherType = Attacher::AttachEngine3D
  FirstAngle = 0
  Height = 12
  Placement = pos=(-70.2,70,0) rot=(0,0,1;1.5708rad)
  Radius = 5
  SecondAngle = 0
FEATURE [Part::Cylinder] Cylinder332  label="円柱332"
  Angle = 180
  AttacherType = Attacher::AttachEngine3D
  FirstAngle = 0
  Height = 12
  Placement = pos=(1.4,70,0) rot=(0,0,-1;1.5708rad)
  Radius = 5
  SecondAngle = 0
FEATURE [Part::Box] Box444  label="立方体414"
  AttacherType = Attacher::AttachEngine3D
  Height = 12
  Length = 2
  Placement = pos=(-0.6,65,0) rot=(0,0,1;0rad)
  Width = 10
FEATURE [Part::Box] Box445  label="立方体415"
  AttacherType = Attacher::AttachEngine3D
  Height = 4
  Length = 14
  Placement = pos=(-40.4,65,0) rot=(0,0,1;0rad)
  Width = 10
FEATURE [Part::RuledSurface] Ruled_Surface
  Curve1 = -> Box445 [Edge3]
  Curve2 = -> Box443 [Edge7]
  Orientation = 0
FEATURE [Part::Extrusion] Extrude
  Base = -> Ruled_Surface
  Dir = (0,1,0)
  DirMode = 0
  FaceMakerClass = Part::FaceMakerBullseye
  FaceMakerMode = 3
  LengthFwd = 0
  LengthRev = 10
  Solid = false
  Symmetric = false
FEATURE [Part::Cylinder] Cylinder333  label="円柱333"
  Angle = 360
  AttacherType = Attacher::AttachEngine3D
  FirstAngle = 0
  Height = 20.5
  Placement = pos=(-10.9,75,2) rot=(1,0,0;1.5708rad)
  Radius = 6
  SecondAngle = 0
FEATURE [Part::RuledSurface] Ruled_Surface001
  Curve1 = -> Box444 [Edge3]
  Curve2 = -> Box445 [Edge7]
  Orientation = 0
FEATURE [Part::Extrusion] Extrude011
  Base = -> Ruled_Surface001
  Dir = (0,1,0)
  DirMode = 0
  FaceMakerClass = Part::FaceMakerBullseye
  FaceMakerMode = 3
  LengthFwd = 0
  LengthRev = 10
  Solid = false
  Symmetric = false
FEATURE [Part::Cylinder] Cylinder335  label="円柱335"
  Angle = 360
  AttacherType = Attacher::AttachEngine3D
  FirstAngle = 0
  Height = 12
  Placement = pos=(-70.2,70,0) rot=(0,0,1;1.5708rad)
  Radius = 2.1
  SecondAngle = 0
FEATURE [Part::Cylinder] Cylinder336  label="円柱336"
  Angle = 360
  AttacherType = Attacher::AttachEngine3D
  FirstAngle = 0
  Height = 12
  Placement = pos=(1.4,70,0) rot=(0,0,-1;1.5708rad)
  Radius = 2.1
  SecondAngle = 0
FEATURE [Part::MultiFuse] Fusion341
  Refine = true
  Shapes = -> [Cylinder332,Box444,Extrude011,Box445,Extrude,Box443,Cylinder331]
FEATURE [Part::Box] Box446  label="立方体416"
  AttacherType = Attacher::AttachEngine3D
  Height = 5
  Length = 70
  Placement = pos=(-69,52,-5) rot=(0,0,1;0rad)
  Width = 24
FEATURE [Part::MultiFuse] Fusion344
  Refine = true
  Shapes = -> [Cylinder335,Cylinder336]
FEATURE [Part::Cylinder] Cylinder334  label="円柱334"
  Angle = 360
  AttacherType = Attacher::AttachEngine3D
  FirstAngle = 0
  Height = 20.5
  Placement = pos=(-56.9,75,2) rot=(1,0,0;1.5708rad)
  Radius = 6
  SecondAngle = 0
FEATURE [Part::MultiFuse] Fusion345
  Refine = true
  Shapes = -> [Cylinder333,Cylinder334]
FEATURE [Part::Cut] Cut352
  Base = -> Fusion345
  Refine = true
  Tool = -> Box446
FEATURE [Part::Cut] Cut353
  Base = -> Fusion341
  Refine = true
  Tool = -> Fusion344
FEATURE [Part::MultiFuse] Fusion346
  Refine = true
  Shapes = -> [Cut353,Cut352]
FEATURE [Part::Box] Box447  label="立方体417"
  AttacherType = Attacher::AttachEngine3D
  Height = 35
  Length = 45.1
  Placement = pos=(-34,-146,-17) rot=(0,0,1;0rad)
  Width = 25
FEATURE [Part::Box] Box448  label="立方体418"
  AttacherType = Attacher::AttachEngine3D
  Height = 32.7
  Length = 12.1
  Placement = pos=(0,8.5,-4.9) rot=(0,0,1;0rad)
  Width = 2.5
FEATURE [Part::Box] Box449  label="立方体419"
  AttacherType = Attacher::AttachEngine3D
  Height = 22.7
  Length = 12.1
  Width = 26.7
FEATURE [Part::Box] Box450  label="立方体420"
  AttacherType = Attacher::AttachEngine3D
  Height = 35
  Length = 12.1
  Placement = pos=(-1,-135,-17) rot=(0,0,1;0rad)
  Width = 14
FEATURE [Part::Cone] Cone004  label="円錐004"
  Angle = 360
  AttacherType = Attacher::AttachEngine3D
  Height = 7
  Radius1 = 38
  Radius2 = 29
FEATURE [Part::Cone] Cone005  label="円錐005"
  Angle = 360
  AttacherType = Attacher::AttachEngine3D
  Height = 7
  Radius1 = 33
  Radius2 = 26
FEATURE [Part::Cut] Cut355
  Base = -> Cone004
  Placement = pos=(-34,-145,-22) rot=(0,0,1;0rad)
  Tool = -> Cone005
FEATURE [Part::Cylinder] Cylinder337  label="円柱337"
  Angle = 360
  AttacherType = Attacher::AttachEngine3D
  FirstAngle = 0
  Height = 50
  Radius = 1.05
  SecondAngle = 0
FEATURE [Part::Cylinder] Cylinder338  label="円柱338"
  Angle = 360
  AttacherType = Attacher::AttachEngine3D
  FirstAngle = 0
  Height = 20
  Placement = pos=(-57,-145,-26) rot=(0,-1,0;0.785398rad)
  Radius = 1.5
  SecondAngle = 0
FEATURE [Part::Cylinder] Cylinder339  label="円柱339"
  Angle = 360
  AttacherType = Attacher::AttachEngine3D
  FirstAngle = 0
  Height = 20
  Placement = pos=(-11,-145,-26) rot=(0,1,0;0.785398rad)
  Radius = 1
  SecondAngle = 0
FEATURE [Part::Cylinder] Cylinder340  label="円柱340"
  Angle = 360
  AttacherType = Attacher::AttachEngine3D
  FirstAngle = 0
  Height = 3
  Placement = pos=(6.05,0,16.4) rot=(1,0,0;1.5708rad)
  Radius = 2.4
  SecondAngle = 0
FEATURE [Part::Cylinder] Cylinder341  label="円柱341"
  Angle = 360
  AttacherType = Attacher::AttachEngine3D
  FirstAngle = 0
  Height = 50
  Placement = pos=(0,-27.7,0) rot=(0,0,1;0rad)
  Radius = 1.05
  SecondAngle = 0
FEATURE [Part::Cylinder] Cylinder342  label="円柱342"
  Angle = 360
  AttacherType = Attacher::AttachEngine3D
  FirstAngle = 0
  Height = 40
  Placement = pos=(-34,-145,-15) rot=(0,0,1;0rad)
  Radius = 29
  SecondAngle = 0
FEATURE [Part::Cylinder] Cylinder343  label="円柱343"
  Angle = 360
  AttacherType = Attacher::AttachEngine3D
  FirstAngle = 0
  Height = 40
  Placement = pos=(-34,-145,-27) rot=(0,0,1;0rad)
  Radius = 26
  SecondAngle = 0
FEATURE [Part::Cylinder] Cylinder344  label="円柱344"
  Angle = 90
  AttacherType = Attacher::AttachEngine3D
  FirstAngle = 0
  Height = 40
  Radius = 29
  SecondAngle = 0
FEATURE [Part::Cylinder] Cylinder345  label="円柱345"
  Angle = 90
  AttacherType = Attacher::AttachEngine3D
  FirstAngle = 0
  Height = 40
  Radius = 35
  SecondAngle = 0
FEATURE [Part::Cut] Cut329
  Base = -> Cylinder345
  Placement = pos=(-34,-145,-17) rot=(0,0,1;0rad)
  Tool = -> Cylinder344
FEATURE [Part::MultiFuse] Fusion347
  Placement = pos=(-1,-151,-12) rot=(0,0,1;0rad)
  Shapes = -> [Cylinder340,Box448,Box449]
FEATURE [Part::MultiFuse] Fusion348
  Placement = pos=(4.1,-111,13.1) rot=(1,0,0;1.5708rad)
  Shapes = -> [Cylinder337,Cylinder341]
FEATURE [Part::MultiFuse] Fusion303
  Placement = pos=(92.57,-66.51,0) rot=(0,0,-1;0.785398rad)
  Shapes = -> [Cylinder339,Cylinder338]
FEATURE [Part::MultiFuse] Fusion350
  Placement = pos=(-30.8902,3.9004,0) rot=(0,0,1;0.20944rad)
  Refine = true
  Shapes = -> [Fusion303]
FEATURE [Part::Sphere] Sphere007  label="球体007"
  Angle1 = 0
  Angle2 = 60
  Angle3 = 360
  AttacherType = Attacher::AttachEngine3D
  Placement = pos=(-34,-145,25) rot=(0,0,1;0rad)
  Radius = 29
FEATURE [Part::Sphere] Sphere008  label="球体008"
  Angle1 = 0
  Angle2 = 60
  Angle3 = 360
  AttacherType = Attacher::AttachEngine3D
  Placement = pos=(-34,-145,13) rot=(0,0,1;0rad)
  Radius = 26
FEATURE [Part::MultiFuse] Fusion349
  Placement = pos=(0,0,12) rot=(0,0,1;0rad)
  Shapes = -> [Cylinder343,Sphere008]
FEATURE [Part::Sphere] Sphere010  label="球体010"
  Angle1 = -90
  Angle2 = 90
  Angle3 = 360
  AttacherType = Attacher::AttachEngine3D
  Placement = pos=(-34,-119,-36) rot=(0,0,1;0rad)
  Radius = 30
FEATURE [Part::Box] Box451  label="立方体421"
  AttacherType = Attacher::AttachEngine3D
  Height = 67
  Length = 15
  Placement = pos=(-24.3,-155,15) rot=(0,0,1;0rad)
  Width = 39
FEATURE [Part::Chamfer] Chamfer040
  Base = -> Box451
  EdgeLinks = -> Box451 [Edge10]
  Edges = 1 edges r=30: [Edge10]
FEATURE [Part::Cylinder] Cylinder346  label="円柱346"
  Angle = 360
  AttacherType = Attacher::AttachEngine3D
  FirstAngle = 0
  Height = 50
  Placement = pos=(-36,-132,56) rot=(0.57735,0.57735,0.57735;2.0944rad)
  Radius = 7
  SecondAngle = 0
FEATURE [Part::Cylinder] Cylinder347  label="円柱347"
  Angle = 360
  AttacherType = Attacher::AttachEngine3D
  FirstAngle = 0
  Height = 40
  Placement = pos=(-34,-145,-27) rot=(0,0,1;0rad)
  Radius = 26
  SecondAngle = 0
FEATURE [Part::Cylinder] Cylinder348  label="円柱348"
  Angle = 90
  AttacherType = Attacher::AttachEngine3D
  FirstAngle = 0
  Height = 79
  Radius = 29
  SecondAngle = 0
FEATURE [Part::Cylinder] Cylinder349  label="円柱349"
  Angle = 90
  AttacherType = Attacher::AttachEngine3D
  FirstAngle = 0
  Height = 79
  Radius = 50
  SecondAngle = 0
FEATURE [Part::Cut] Cut359
  Base = -> Cylinder349
  Placement = pos=(-34,-145,-17) rot=(0,0,1;0rad)
  Tool = -> Cylinder348
FEATURE [Part::Sphere] Sphere009  label="球体009"
  Angle1 = 0
  Angle2 = 60
  Angle3 = 360
  AttacherType = Attacher::AttachEngine3D
  Placement = pos=(-34,-145,13) rot=(0,0,1;0rad)
  Radius = 26
FEATURE [Part::MultiFuse] Fusion302
  Placement = pos=(0,0,17) rot=(0,0,1;0rad)
  Shapes = -> [Cylinder347,Sphere009]
FEATURE [Part::Box] Box452  label="立方体422"
  AttacherType = Attacher::AttachEngine3D
  Height = 20
  Length = 15
  Placement = pos=(-26.6,-113,62) rot=(0,0,1;0rad)
  Width = 24
FEATURE [Part::Cylinder] Cylinder350  label="円柱350"
  Angle = 360
  AttacherType = Attacher::AttachEngine3D
  FirstAngle = 0
  Height = 15
  Placement = pos=(-26.6,-89,72) rot=(0.57735,0.57735,0.57735;2.0944rad)
  Radius = 10
  SecondAngle = 0
FEATURE [Part::Cylinder] Cylinder351  label="円柱351"
  Angle = 360
  AttacherType = Attacher::AttachEngine3D
  FirstAngle = 0
  Height = 25
  Placement = pos=(-31.3,-89,72) rot=(0.57735,0.57735,0.57735;2.0944rad)
  Radius = 1.6
  SecondAngle = 0
FEATURE [Part::Chamfer] Chamfer043
  Base = -> Cut355
  EdgeLinks = -> Cut355 [Edge3]
  Edges = 1 edges r=2: [Edge3]
FEATURE [Part::Chamfer] Chamfer041
  Base = -> Chamfer040
  EdgeLinks = -> Chamfer040 [Edge2,Edge6,Edge7,Edge10]
  Edges = 4 edges r=5: [Edge2,Edge6,Edge7,Edge10]
  Placement = pos=(-2.3,0,0) rot=(0,0,1;0rad)
FEATURE [Part::MultiFuse] Fusion355
  Refine = true
  Shapes = -> [Box452,Cylinder350]
FEATURE [Part::Box] Box453  label="立方体423"
  AttacherType = Attacher::AttachEngine3D
  Height = 13
  Length = 7
  Placement = pos=(-26.6,-113,65.5) rot=(0,0,1;0rad)
  Width = 34
FEATURE [Part::MultiFuse] Fusion358
  Shapes = -> [Chamfer043,Cylinder342,Sphere007]
FEATURE [Part::Cut] Cut372
  Base = -> Fusion358
  Tool = -> Sphere010
FEATURE [Part::Cut] Cut373
  Base = -> Cut372
  Tool = -> Fusion350
FEATURE [Part::Cut] Cut375
  Base = -> Chamfer041
  Tool = -> Cylinder346
FEATURE [Part::Cut] Cut376
  Base = -> Cut375
  Tool = -> Cut359
FEATURE [Part::Cut] Cut377
  Base = -> Cut376
  Tool = -> Fusion302
FEATURE [Part::Cut] Cut378
  Base = -> Fusion355
  Tool = -> Cylinder351
FEATURE [Part::Cut] Cut379
  Base = -> Cut378
  Tool = -> Box453
FEATURE [Part::Cut] Cut380
  Base = -> Box447
  Tool = -> Fusion347
FEATURE [Part::Cut] Cut381
  Base = -> Cut380
  Tool = -> Box450
FEATURE [Part::Cut] Cut382
  Base = -> Cut381
  Placement = pos=(-4,-10,2) rot=(0,0,1;0rad)
  Tool = -> Fusion348
FEATURE [Part::Cut] Cut383
  Base = -> Cut382
  Tool = -> Cut329
FEATURE [Part::MultiFuse] Fusion359
  Shapes = -> [Cut383,Cut373]
FEATURE [Part::Cut] Cut384
  Base = -> Fusion359
  Placement = pos=(0,0,5) rot=(0,0,1;0rad)
  Tool = -> Fusion349
FEATURE [Part::MultiFuse] Fusion360
  Placement = pos=(0,3,0) rot=(0,0,1;0rad)
  Shapes = -> [Cut377,Cut384]
FEATURE [Part::MultiFuse] Fusion361
  Shapes = -> [Cut379,Fusion360]
